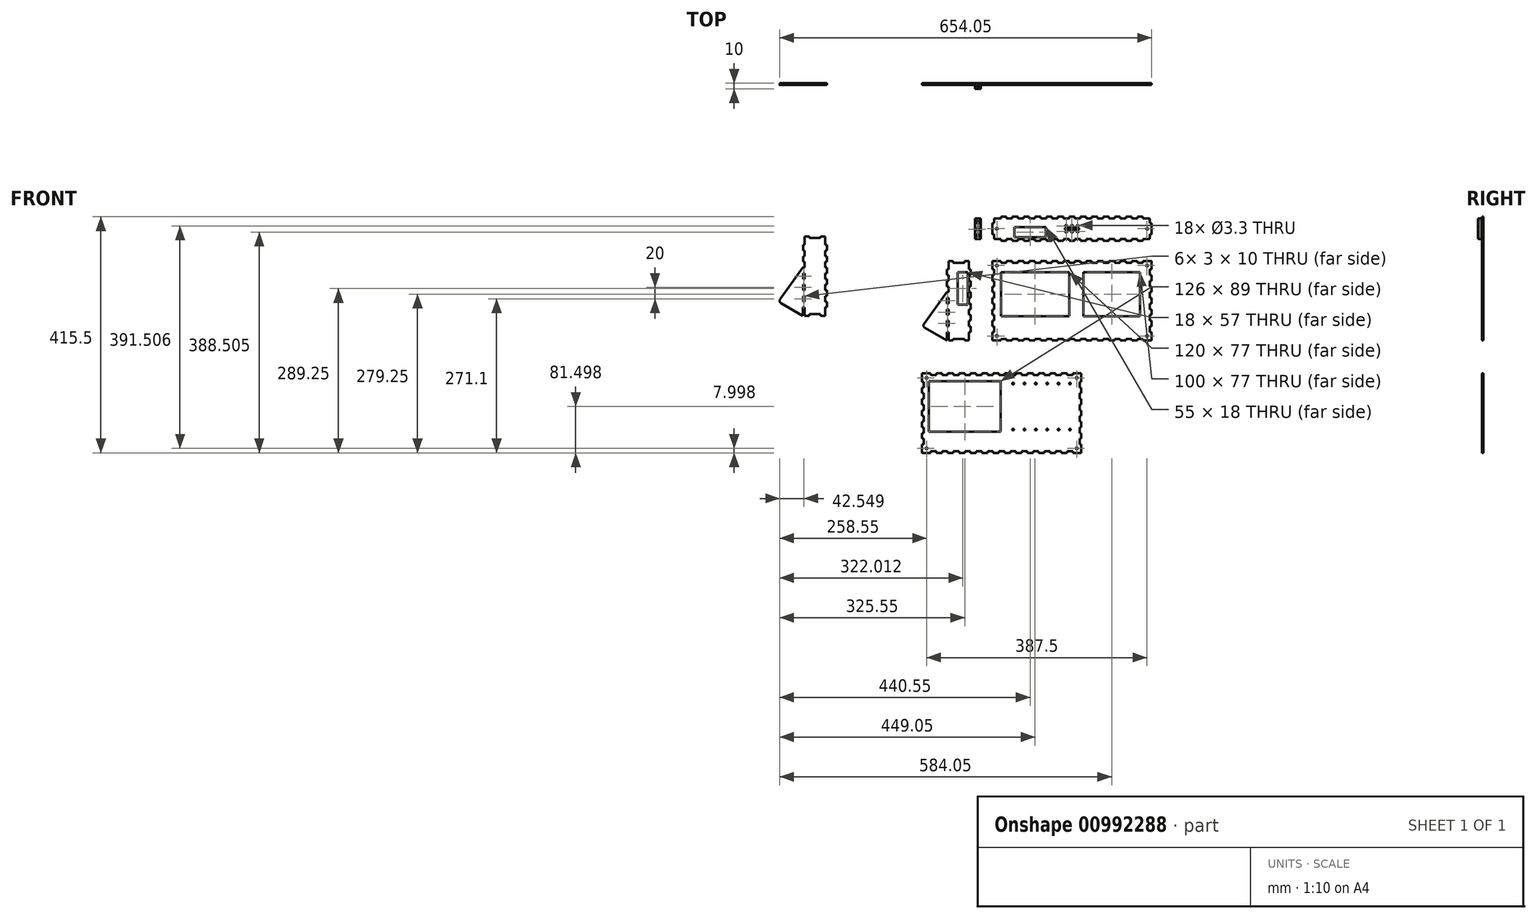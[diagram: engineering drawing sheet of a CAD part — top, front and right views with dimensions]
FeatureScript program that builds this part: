
annotation { "Feature Type Name" : "Feature", "Feature Type Description" : "" }
export const myFeature = defineFeature(function(context is Context, id is Id, definition is map)
    precondition{}
    {
        {
            var Q0;
            Q0=qCreatedBy(makeId("Front.planeOp"),FACE);
            var sketch = newSketch(context, id + "F0", { "sketchPlane" : qUnion([Q0])});
            skLineSegment(sketch, "E0.bottom", {"start": v(-60, 38.5) * mm, "end": v(60, 38.5) * mm});
            skLineSegment(sketch, "E0.top", {"start": v(-60, -38.5) * mm, "end": v(60, -38.5) * mm});
            skLineSegment(sketch, "E0.left", {"start": v(-60, 38.5) * mm, "end": v(-60, -38.5) * mm});
            skLineSegment(sketch, "E0.right", {"start": v(60, 38.5) * mm, "end": v(60, -38.5) * mm});
            skPoint(sketch, "E0.middle", {"position": v(0, 0) * mm});
            skLineSegment(sketch, "E1.bottom", {"start": v(-75, -81.5) * mm, "end": v(-60, -81.5) * mm});
            skLineSegment(sketch, "E1.top", {"start": v(-75, 58.5) * mm, "end": v(-60, 58.5) * mm});
            skLineSegment(sketch, "E1.left", {"start": v(-75, -81.5) * mm, "end": v(-75, -66.5) * mm});
            skLineSegment(sketch, "E1.right", {"start": v(205, -81.5) * mm, "end": v(205, -66.5) * mm});
            skLineSegment(sketch, "E2.bottom", {"start": v(85, -38.5) * mm, "end": v(185, -38.5) * mm});
            skLineSegment(sketch, "E2.top", {"start": v(85, 38.5) * mm, "end": v(185, 38.5) * mm});
            skLineSegment(sketch, "E2.left", {"start": v(85, -38.5) * mm, "end": v(85, 38.5) * mm});
            skLineSegment(sketch, "E2.right", {"start": v(185, -38.5) * mm, "end": v(185, 38.5) * mm});
            skLineSegment(sketch, "E3", {"start": v(-75, 43.5) * mm, "end": v(-72, 43.5) * mm});
            skLineSegment(sketch, "E4", {"start": v(-72, 43.5) * mm, "end": v(-72, 33.5) * mm});
            skLineSegment(sketch, "E5", {"start": v(-72, 33.5) * mm, "end": v(-75, 33.5) * mm});
            skLineSegment(sketch, "E6.0.1.0", {"start": v(-75, 23.5) * mm, "end": v(-72, 23.5) * mm});
            skLineSegment(sketch, "E6.0.1.1", {"start": v(-72, 23.5) * mm, "end": v(-72, 13.5) * mm});
            skLineSegment(sketch, "E6.0.1.2", {"start": v(-72, 13.5) * mm, "end": v(-75, 13.5) * mm});
            skLineSegment(sketch, "E6.0.2.0", {"start": v(-75, 3.5) * mm, "end": v(-72, 3.5) * mm});
            skLineSegment(sketch, "E6.0.2.1", {"start": v(-72, 3.5) * mm, "end": v(-72, -6.5) * mm});
            skLineSegment(sketch, "E6.0.2.2", {"start": v(-72, -6.5) * mm, "end": v(-75, -6.5) * mm});
            skLineSegment(sketch, "E6.0.3.0", {"start": v(-75, -16.5) * mm, "end": v(-72, -16.5) * mm});
            skLineSegment(sketch, "E6.0.3.1", {"start": v(-72, -16.5) * mm, "end": v(-72, -26.5) * mm});
            skLineSegment(sketch, "E6.0.3.2", {"start": v(-72, -26.5) * mm, "end": v(-75, -26.5) * mm});
            skLineSegment(sketch, "E6.0.4.0", {"start": v(-75, -36.5) * mm, "end": v(-72, -36.5) * mm});
            skLineSegment(sketch, "E6.0.4.1", {"start": v(-72, -36.5) * mm, "end": v(-72, -46.5) * mm});
            skLineSegment(sketch, "E6.0.4.2", {"start": v(-72, -46.5) * mm, "end": v(-75, -46.5) * mm});
            skLineSegment(sketch, "E6.0.5.0", {"start": v(-75, -56.5) * mm, "end": v(-72, -56.5) * mm});
            skLineSegment(sketch, "E6.0.5.1", {"start": v(-72, -56.5) * mm, "end": v(-72, -66.5) * mm});
            skLineSegment(sketch, "E6.0.5.2", {"start": v(-72, -66.5) * mm, "end": v(-75, -66.5) * mm});
            skLineSegment(sketch, "E6.direction1", {"start": v(-75, 43.5) * mm, "end": v(-45, 43.5) * mm, "construction": true});
            skLineSegment(sketch, "E6.direction2", {"start": v(-75, 33.5) * mm, "end": v(-75, 23.5) * mm, "construction": true});
            skLineSegment(sketch, "E7", {"start": v(205, 43.5) * mm, "end": v(202, 43.5) * mm});
            skLineSegment(sketch, "E8", {"start": v(202, 43.5) * mm, "end": v(202, 33.5) * mm});
            skLineSegment(sketch, "E9", {"start": v(202, 33.5) * mm, "end": v(205, 33.5) * mm});
            skLineSegment(sketch, "E10.0.1.0", {"start": v(205, 23.5) * mm, "end": v(202, 23.5) * mm});
            skLineSegment(sketch, "E10.0.1.1", {"start": v(202, 23.5) * mm, "end": v(202, 13.5) * mm});
            skLineSegment(sketch, "E10.0.1.2", {"start": v(202, 13.5) * mm, "end": v(205, 13.5) * mm});
            skLineSegment(sketch, "E10.0.2.0", {"start": v(205, 3.5) * mm, "end": v(202, 3.5) * mm});
            skLineSegment(sketch, "E10.0.2.1", {"start": v(202, 3.5) * mm, "end": v(202, -6.5) * mm});
            skLineSegment(sketch, "E10.0.2.2", {"start": v(202, -6.5) * mm, "end": v(205, -6.5) * mm});
            skLineSegment(sketch, "E10.0.3.0", {"start": v(205, -16.5) * mm, "end": v(202, -16.5) * mm});
            skLineSegment(sketch, "E10.0.3.1", {"start": v(202, -16.5) * mm, "end": v(202, -26.5) * mm});
            skLineSegment(sketch, "E10.0.3.2", {"start": v(202, -26.5) * mm, "end": v(205, -26.5) * mm});
            skLineSegment(sketch, "E10.0.4.0", {"start": v(205, -36.5) * mm, "end": v(202, -36.5) * mm});
            skLineSegment(sketch, "E10.0.4.1", {"start": v(202, -36.5) * mm, "end": v(202, -46.5) * mm});
            skLineSegment(sketch, "E10.0.4.2", {"start": v(202, -46.5) * mm, "end": v(205, -46.5) * mm});
            skLineSegment(sketch, "E10.0.5.0", {"start": v(205, -56.5) * mm, "end": v(202, -56.5) * mm});
            skLineSegment(sketch, "E10.0.5.1", {"start": v(202, -56.5) * mm, "end": v(202, -66.5) * mm});
            skLineSegment(sketch, "E10.0.5.2", {"start": v(202, -66.5) * mm, "end": v(205, -66.5) * mm});
            skLineSegment(sketch, "E10.direction1", {"start": v(202, 43.5) * mm, "end": v(232, 43.5) * mm, "construction": true});
            skLineSegment(sketch, "E10.direction2", {"start": v(202, 43.5) * mm, "end": v(202, 23.5) * mm, "construction": true});
            skLineSegment(sketch, "E11", {"start": v(190, -81.5) * mm, "end": v(190, -78.5) * mm});
            skLineSegment(sketch, "E12", {"start": v(190, -78.5) * mm, "end": v(180, -78.5) * mm});
            skLineSegment(sketch, "E13", {"start": v(180, -78.5) * mm, "end": v(180, -81.5) * mm});
            skLineSegment(sketch, "E14.1.0.0", {"start": v(160, -78.5) * mm, "end": v(160, -81.5) * mm});
            skLineSegment(sketch, "E14.1.0.1", {"start": v(170, -78.5) * mm, "end": v(160, -78.5) * mm});
            skLineSegment(sketch, "E14.1.0.2", {"start": v(170, -81.5) * mm, "end": v(170, -78.5) * mm});
            skLineSegment(sketch, "E14.2.0.0", {"start": v(140, -78.5) * mm, "end": v(140, -81.5) * mm});
            skLineSegment(sketch, "E14.2.0.1", {"start": v(150, -78.5) * mm, "end": v(140, -78.5) * mm});
            skLineSegment(sketch, "E14.2.0.2", {"start": v(150, -81.5) * mm, "end": v(150, -78.5) * mm});
            skLineSegment(sketch, "E14.3.0.0", {"start": v(120, -78.5) * mm, "end": v(120, -81.5) * mm});
            skLineSegment(sketch, "E14.3.0.1", {"start": v(130, -78.5) * mm, "end": v(120, -78.5) * mm});
            skLineSegment(sketch, "E14.3.0.2", {"start": v(130, -81.5) * mm, "end": v(130, -78.5) * mm});
            skLineSegment(sketch, "E14.4.0.0", {"start": v(100, -78.5) * mm, "end": v(100, -81.5) * mm});
            skLineSegment(sketch, "E14.4.0.1", {"start": v(110, -78.5) * mm, "end": v(100, -78.5) * mm});
            skLineSegment(sketch, "E14.4.0.2", {"start": v(110, -81.5) * mm, "end": v(110, -78.5) * mm});
            skLineSegment(sketch, "E14.5.0.0", {"start": v(80, -78.5) * mm, "end": v(80, -81.5) * mm});
            skLineSegment(sketch, "E14.5.0.1", {"start": v(90, -78.5) * mm, "end": v(80, -78.5) * mm});
            skLineSegment(sketch, "E14.5.0.2", {"start": v(90, -81.5) * mm, "end": v(90, -78.5) * mm});
            skLineSegment(sketch, "E14.6.0.0", {"start": v(60, -78.5) * mm, "end": v(60, -81.5) * mm});
            skLineSegment(sketch, "E14.6.0.1", {"start": v(70, -78.5) * mm, "end": v(60, -78.5) * mm});
            skLineSegment(sketch, "E14.6.0.2", {"start": v(70, -81.5) * mm, "end": v(70, -78.5) * mm});
            skLineSegment(sketch, "E14.7.0.0", {"start": v(40, -78.5) * mm, "end": v(40, -81.5) * mm});
            skLineSegment(sketch, "E14.7.0.1", {"start": v(50, -78.5) * mm, "end": v(40, -78.5) * mm});
            skLineSegment(sketch, "E14.7.0.2", {"start": v(50, -81.5) * mm, "end": v(50, -78.5) * mm});
            skLineSegment(sketch, "E14.8.0.0", {"start": v(20, -78.5) * mm, "end": v(20, -81.5) * mm});
            skLineSegment(sketch, "E14.8.0.1", {"start": v(30, -78.5) * mm, "end": v(20, -78.5) * mm});
            skLineSegment(sketch, "E14.8.0.2", {"start": v(30, -81.5) * mm, "end": v(30, -78.5) * mm});
            skLineSegment(sketch, "E14.9.0.0", {"start": v(0, -78.5) * mm, "end": v(0, -81.5) * mm});
            skLineSegment(sketch, "E14.9.0.1", {"start": v(10, -78.5) * mm, "end": v(0, -78.5) * mm});
            skLineSegment(sketch, "E14.9.0.2", {"start": v(10, -81.5) * mm, "end": v(10, -78.5) * mm});
            skLineSegment(sketch, "E14.10.0.0", {"start": v(-20, -78.5) * mm, "end": v(-20, -81.5) * mm});
            skLineSegment(sketch, "E14.10.0.1", {"start": v(-10, -78.5) * mm, "end": v(-20, -78.5) * mm});
            skLineSegment(sketch, "E14.10.0.2", {"start": v(-10, -81.5) * mm, "end": v(-10, -78.5) * mm});
            skLineSegment(sketch, "E14.11.0.0", {"start": v(-40, -78.5) * mm, "end": v(-40, -81.5) * mm});
            skLineSegment(sketch, "E14.11.0.1", {"start": v(-30, -78.5) * mm, "end": v(-40, -78.5) * mm});
            skLineSegment(sketch, "E14.11.0.2", {"start": v(-30, -81.5) * mm, "end": v(-30, -78.5) * mm});
            skLineSegment(sketch, "E14.12.0.0", {"start": v(-60, -78.5) * mm, "end": v(-60, -81.5) * mm});
            skLineSegment(sketch, "E14.12.0.1", {"start": v(-50, -78.5) * mm, "end": v(-60, -78.5) * mm});
            skLineSegment(sketch, "E14.12.0.2", {"start": v(-50, -81.5) * mm, "end": v(-50, -78.5) * mm});
            skLineSegment(sketch, "E14.direction1", {"start": v(180, -81.5) * mm, "end": v(170, -81.5) * mm, "construction": true});
            skLineSegment(sketch, "E15", {"start": v(190, 58.5) * mm, "end": v(190, 55.5) * mm});
            skLineSegment(sketch, "E16", {"start": v(190, 55.5) * mm, "end": v(180, 55.5) * mm});
            skLineSegment(sketch, "E17", {"start": v(180, 55.5) * mm, "end": v(180, 58.5) * mm});
            skLineSegment(sketch, "E18.1.0.0", {"start": v(170, 55.5) * mm, "end": v(160, 55.5) * mm});
            skLineSegment(sketch, "E18.1.0.1", {"start": v(170, 58.5) * mm, "end": v(170, 55.5) * mm});
            skLineSegment(sketch, "E18.1.0.2", {"start": v(160, 55.5) * mm, "end": v(160, 58.5) * mm});
            skLineSegment(sketch, "E18.2.0.0", {"start": v(150, 55.5) * mm, "end": v(140, 55.5) * mm});
            skLineSegment(sketch, "E18.2.0.1", {"start": v(150, 58.5) * mm, "end": v(150, 55.5) * mm});
            skLineSegment(sketch, "E18.2.0.2", {"start": v(140, 55.5) * mm, "end": v(140, 58.5) * mm});
            skLineSegment(sketch, "E18.3.0.0", {"start": v(130, 55.5) * mm, "end": v(120, 55.5) * mm});
            skLineSegment(sketch, "E18.3.0.1", {"start": v(130, 58.5) * mm, "end": v(130, 55.5) * mm});
            skLineSegment(sketch, "E18.3.0.2", {"start": v(120, 55.5) * mm, "end": v(120, 58.5) * mm});
            skLineSegment(sketch, "E18.4.0.0", {"start": v(110, 55.5) * mm, "end": v(100, 55.5) * mm});
            skLineSegment(sketch, "E18.4.0.1", {"start": v(110, 58.5) * mm, "end": v(110, 55.5) * mm});
            skLineSegment(sketch, "E18.4.0.2", {"start": v(100, 55.5) * mm, "end": v(100, 58.5) * mm});
            skLineSegment(sketch, "E18.5.0.0", {"start": v(90, 55.5) * mm, "end": v(80, 55.5) * mm});
            skLineSegment(sketch, "E18.5.0.1", {"start": v(90, 58.5) * mm, "end": v(90, 55.5) * mm});
            skLineSegment(sketch, "E18.5.0.2", {"start": v(80, 55.5) * mm, "end": v(80, 58.5) * mm});
            skLineSegment(sketch, "E18.6.0.0", {"start": v(70, 55.5) * mm, "end": v(60, 55.5) * mm});
            skLineSegment(sketch, "E18.6.0.1", {"start": v(70, 58.5) * mm, "end": v(70, 55.5) * mm});
            skLineSegment(sketch, "E18.6.0.2", {"start": v(60, 55.5) * mm, "end": v(60, 58.5) * mm});
            skLineSegment(sketch, "E18.7.0.0", {"start": v(50, 55.5) * mm, "end": v(40, 55.5) * mm});
            skLineSegment(sketch, "E18.7.0.1", {"start": v(50, 58.5) * mm, "end": v(50, 55.5) * mm});
            skLineSegment(sketch, "E18.7.0.2", {"start": v(40, 55.5) * mm, "end": v(40, 58.5) * mm});
            skLineSegment(sketch, "E18.8.0.0", {"start": v(30, 55.5) * mm, "end": v(20, 55.5) * mm});
            skLineSegment(sketch, "E18.8.0.1", {"start": v(30, 58.5) * mm, "end": v(30, 55.5) * mm});
            skLineSegment(sketch, "E18.8.0.2", {"start": v(20, 55.5) * mm, "end": v(20, 58.5) * mm});
            skLineSegment(sketch, "E18.9.0.0", {"start": v(10, 55.5) * mm, "end": v(0, 55.5) * mm});
            skLineSegment(sketch, "E18.9.0.1", {"start": v(10, 58.5) * mm, "end": v(10, 55.5) * mm});
            skLineSegment(sketch, "E18.9.0.2", {"start": v(0, 55.5) * mm, "end": v(0, 58.5) * mm});
            skLineSegment(sketch, "E18.10.0.0", {"start": v(-10, 55.5) * mm, "end": v(-20, 55.5) * mm});
            skLineSegment(sketch, "E18.10.0.1", {"start": v(-10, 58.5) * mm, "end": v(-10, 55.5) * mm});
            skLineSegment(sketch, "E18.10.0.2", {"start": v(-20, 55.5) * mm, "end": v(-20, 58.5) * mm});
            skLineSegment(sketch, "E18.11.0.0", {"start": v(-30, 55.5) * mm, "end": v(-40, 55.5) * mm});
            skLineSegment(sketch, "E18.11.0.1", {"start": v(-30, 58.5) * mm, "end": v(-30, 55.5) * mm});
            skLineSegment(sketch, "E18.11.0.2", {"start": v(-40, 55.5) * mm, "end": v(-40, 58.5) * mm});
            skLineSegment(sketch, "E18.12.0.0", {"start": v(-50, 55.5) * mm, "end": v(-60, 55.5) * mm});
            skLineSegment(sketch, "E18.12.0.1", {"start": v(-50, 58.5) * mm, "end": v(-50, 55.5) * mm});
            skLineSegment(sketch, "E18.12.0.2", {"start": v(-60, 55.5) * mm, "end": v(-60, 58.5) * mm});
            skLineSegment(sketch, "E18.direction1", {"start": v(180, 55.5) * mm, "end": v(160, 55.5) * mm, "construction": true});
            skLineSegment(sketch, "E19.trimOffspring", {"start": v(-50, 58.5) * mm, "end": v(-40, 58.5) * mm});
            skLineSegment(sketch, "E20.trimOffspring", {"start": v(-30, 58.5) * mm, "end": v(-20, 58.5) * mm});
            skLineSegment(sketch, "E21.trimOffspring", {"start": v(-10, 58.5) * mm, "end": v(0, 58.5) * mm});
            skLineSegment(sketch, "E22.trimOffspring", {"start": v(10, 58.5) * mm, "end": v(20, 58.5) * mm});
            skLineSegment(sketch, "E23.trimOffspring", {"start": v(30, 58.5) * mm, "end": v(40, 58.5) * mm});
            skLineSegment(sketch, "E24.trimOffspring", {"start": v(50, 58.5) * mm, "end": v(60, 58.5) * mm});
            skLineSegment(sketch, "E25.trimOffspring", {"start": v(70, 58.5) * mm, "end": v(80, 58.5) * mm});
            skLineSegment(sketch, "E26.trimOffspring", {"start": v(90, 58.5) * mm, "end": v(100, 58.5) * mm});
            skLineSegment(sketch, "E27.trimOffspring", {"start": v(110, 58.5) * mm, "end": v(120, 58.5) * mm});
            skLineSegment(sketch, "E28.trimOffspring", {"start": v(-75, 23.5) * mm, "end": v(-75, 33.5) * mm});
            skLineSegment(sketch, "E29.trimOffspring", {"start": v(130, 58.5) * mm, "end": v(140, 58.5) * mm});
            skLineSegment(sketch, "E30.trimOffspring", {"start": v(150, 58.5) * mm, "end": v(160, 58.5) * mm});
            skLineSegment(sketch, "E31.trimOffspring", {"start": v(170, 58.5) * mm, "end": v(180, 58.5) * mm});
            skLineSegment(sketch, "E32.trimOffspring", {"start": v(190, 58.5) * mm, "end": v(205, 58.5) * mm});
            skLineSegment(sketch, "E33.trimOffspring", {"start": v(205, 43.5) * mm, "end": v(205, 58.5) * mm});
            skLineSegment(sketch, "E34.trimOffspring", {"start": v(205, 23.5) * mm, "end": v(205, 33.5) * mm});
            skLineSegment(sketch, "E35.trimOffspring", {"start": v(205, 3.5) * mm, "end": v(205, 13.5) * mm});
            skLineSegment(sketch, "E36.trimOffspring", {"start": v(205, -16.5) * mm, "end": v(205, -6.5) * mm});
            skLineSegment(sketch, "E37.trimOffspring", {"start": v(205, -56.5) * mm, "end": v(205, -46.5) * mm});
            skLineSegment(sketch, "E38.trimOffspring", {"start": v(205, -36.5) * mm, "end": v(205, -26.5) * mm});
            skLineSegment(sketch, "E39.trimOffspring", {"start": v(190, -81.5) * mm, "end": v(205, -81.5) * mm});
            skLineSegment(sketch, "E40.trimOffspring", {"start": v(150, -81.5) * mm, "end": v(160, -81.5) * mm});
            skLineSegment(sketch, "E41.trimOffspring", {"start": v(130, -81.5) * mm, "end": v(140, -81.5) * mm});
            skLineSegment(sketch, "E42.trimOffspring", {"start": v(110, -81.5) * mm, "end": v(120, -81.5) * mm});
            skLineSegment(sketch, "E43.trimOffspring", {"start": v(170, -81.5) * mm, "end": v(180, -81.5) * mm});
            skLineSegment(sketch, "E44.trimOffspring", {"start": v(90, -81.5) * mm, "end": v(100, -81.5) * mm});
            skLineSegment(sketch, "E45.trimOffspring", {"start": v(70, -81.5) * mm, "end": v(80, -81.5) * mm});
            skLineSegment(sketch, "E46.trimOffspring", {"start": v(50, -81.5) * mm, "end": v(60, -81.5) * mm});
            skLineSegment(sketch, "E47.trimOffspring", {"start": v(30, -81.5) * mm, "end": v(40, -81.5) * mm});
            skLineSegment(sketch, "E48.trimOffspring", {"start": v(10, -81.5) * mm, "end": v(20, -81.5) * mm});
            skLineSegment(sketch, "E49.trimOffspring", {"start": v(-10, -81.5) * mm, "end": v(0, -81.5) * mm});
            skLineSegment(sketch, "E50.trimOffspring", {"start": v(-30, -81.5) * mm, "end": v(-20, -81.5) * mm});
            skLineSegment(sketch, "E51.trimOffspring", {"start": v(-50, -81.5) * mm, "end": v(-40, -81.5) * mm});
            skLineSegment(sketch, "E52.trimOffspring", {"start": v(-75, -56.5) * mm, "end": v(-75, -46.5) * mm});
            skLineSegment(sketch, "E53.trimOffspring", {"start": v(-75, -36.5) * mm, "end": v(-75, -26.5) * mm});
            skLineSegment(sketch, "E54.trimOffspring", {"start": v(-75, -16.5) * mm, "end": v(-75, -6.5) * mm});
            skLineSegment(sketch, "E55.trimOffspring", {"start": v(-75, 3.5) * mm, "end": v(-75, 13.5) * mm});
            skLineSegment(sketch, "E56.trimOffspring", {"start": v(-75, 43.5) * mm, "end": v(-75, 58.5) * mm});
            skLineSegment(sketch, "E57.bottom", {"start": v(-116.04, 58.5) * mm, "end": v(-124.04, 58.5) * mm});
            skLineSegment(sketch, "E57.top", {"start": v(-116.04, -81.5) * mm, "end": v(-124.04, -81.5) * mm});
            skLineSegment(sketch, "E57.left", {"start": v(-116.04, 58.5) * mm, "end": v(-116.04, 43.5) * mm});
            skLineSegment(sketch, "E57.right", {"start": v(-152.04, 58.5) * mm, "end": v(-152.04, 43.5) * mm});
            skLineSegment(sketch, "E58", {"start": v(-116.04, 43.5) * mm, "end": v(-113.04, 43.5) * mm});
            skLineSegment(sketch, "E59", {"start": v(-113.04, 43.5) * mm, "end": v(-113.04, 33.5) * mm});
            skLineSegment(sketch, "E60", {"start": v(-113.04, 33.5) * mm, "end": v(-116.04, 33.5) * mm});
            skLineSegment(sketch, "E61.0.1.0", {"start": v(-116.04, 23.5) * mm, "end": v(-113.04, 23.5) * mm});
            skLineSegment(sketch, "E61.0.1.1", {"start": v(-113.04, 23.5) * mm, "end": v(-113.04, 13.5) * mm});
            skLineSegment(sketch, "E61.0.1.2", {"start": v(-113.04, 13.5) * mm, "end": v(-116.04, 13.5) * mm});
            skLineSegment(sketch, "E61.0.2.0", {"start": v(-116.04, 3.5) * mm, "end": v(-113.04, 3.5) * mm});
            skLineSegment(sketch, "E61.0.2.1", {"start": v(-113.04, 3.5) * mm, "end": v(-113.04, -6.5) * mm});
            skLineSegment(sketch, "E61.0.2.2", {"start": v(-113.04, -6.5) * mm, "end": v(-116.04, -6.5) * mm});
            skLineSegment(sketch, "E61.0.3.0", {"start": v(-116.04, -16.5) * mm, "end": v(-113.04, -16.5) * mm});
            skLineSegment(sketch, "E61.0.3.1", {"start": v(-113.04, -16.5) * mm, "end": v(-113.04, -26.5) * mm});
            skLineSegment(sketch, "E61.0.3.2", {"start": v(-113.04, -26.5) * mm, "end": v(-116.04, -26.5) * mm});
            skLineSegment(sketch, "E61.0.4.0", {"start": v(-116.04, -36.5) * mm, "end": v(-113.04, -36.5) * mm});
            skLineSegment(sketch, "E61.0.4.1", {"start": v(-113.04, -36.5) * mm, "end": v(-113.04, -46.5) * mm});
            skLineSegment(sketch, "E61.0.4.2", {"start": v(-113.04, -46.5) * mm, "end": v(-116.04, -46.5) * mm});
            skLineSegment(sketch, "E61.0.5.0", {"start": v(-116.04, -56.5) * mm, "end": v(-113.04, -56.5) * mm});
            skLineSegment(sketch, "E61.0.5.1", {"start": v(-113.04, -56.5) * mm, "end": v(-113.04, -66.5) * mm});
            skLineSegment(sketch, "E61.0.5.2", {"start": v(-113.04, -66.5) * mm, "end": v(-116.04, -66.5) * mm});
            skLineSegment(sketch, "E61.direction1", {"start": v(-116.04, 43.5) * mm, "end": v(-91.04, 43.5) * mm, "construction": true});
            skLineSegment(sketch, "E61.direction2", {"start": v(-116.04, 33.5) * mm, "end": v(-116.04, 23.5) * mm, "construction": true});
            skLineSegment(sketch, "E62.trimOffspring", {"start": v(-116.04, 13.5) * mm, "end": v(-116.04, 3.5) * mm});
            skLineSegment(sketch, "E63.trimOffspring", {"start": v(-116.04, 33.5) * mm, "end": v(-116.04, 23.5) * mm});
            skLineSegment(sketch, "E64.trimOffspring", {"start": v(-116.04, -6.5) * mm, "end": v(-116.04, -16.5) * mm});
            skLineSegment(sketch, "E65.trimOffspring", {"start": v(-116.04, -26.5) * mm, "end": v(-116.04, -36.5) * mm});
            skLineSegment(sketch, "E66.trimOffspring", {"start": v(-116.04, -46.5) * mm, "end": v(-116.04, -56.5) * mm});
            skLineSegment(sketch, "E67.trimOffspring", {"start": v(-116.04, -66.5) * mm, "end": v(-116.04, -81.5) * mm});
            skLineSegment(sketch, "E68", {"start": v(-152.04, 43.5) * mm, "end": v(-155.04, 43.5) * mm});
            skLineSegment(sketch, "E69", {"start": v(-155.04, 43.5) * mm, "end": v(-155.04, 33.5) * mm});
            skLineSegment(sketch, "E70", {"start": v(-155.04, 33.5) * mm, "end": v(-152.04, 33.5) * mm});
            skLineSegment(sketch, "E71.0.1.0", {"start": v(-152.04, 23.5) * mm, "end": v(-155.04, 23.5) * mm});
            skLineSegment(sketch, "E71.0.1.1", {"start": v(-155.04, 23.5) * mm, "end": v(-155.04, 13.5) * mm});
            skLineSegment(sketch, "E71.0.1.2", {"start": v(-155.04, 13.5) * mm, "end": v(-152.04, 13.5) * mm});
            skLineSegment(sketch, "E71.0.2.0", {"start": v(-152.04, 3.5) * mm, "end": v(-155.04, 3.5) * mm});
            skLineSegment(sketch, "E71.0.2.2", {"start": v(-155.04, -6.5) * mm, "end": v(-152.04, -6.5) * mm});
            skLineSegment(sketch, "E71.0.3.0", {"start": v(-152.04, -16.5) * mm, "end": v(-155.04, -16.5) * mm});
            skLineSegment(sketch, "E71.0.3.2", {"start": v(-155.04, -26.5) * mm, "end": v(-152.04, -26.5) * mm});
            skLineSegment(sketch, "E71.0.4.0", {"start": v(-152.04, -36.5) * mm, "end": v(-155.04, -36.5) * mm});
            skLineSegment(sketch, "E71.0.4.2", {"start": v(-155.04, -46.5) * mm, "end": v(-152.04, -46.5) * mm});
            skLineSegment(sketch, "E71.0.5.0", {"start": v(-152.04, -56.5) * mm, "end": v(-155.04, -56.5) * mm});
            skLineSegment(sketch, "E71.0.5.2", {"start": v(-155.04, -66.5) * mm, "end": v(-152.04, -66.5) * mm});
            skLineSegment(sketch, "E71.direction1", {"start": v(-155.04, 43.5) * mm, "end": v(-130.04, 43.5) * mm, "construction": true});
            skLineSegment(sketch, "E71.direction2", {"start": v(-155.04, 43.5) * mm, "end": v(-155.04, 23.5) * mm, "construction": true});
            skLineSegment(sketch, "E72.trimOffspring", {"start": v(-152.04, 33.5) * mm, "end": v(-152.04, 23.5) * mm});
            skLineSegment(sketch, "E73.trimOffspring", {"start": v(-152.04, 13.5) * mm, "end": v(-152.04, 3.5) * mm});
            skLineSegment(sketch, "E74.trimOffspring", {"start": v(-152.04, -6.5) * mm, "end": v(-152.04, -16.5) * mm});
            skLineSegment(sketch, "E75", {"start": v(-155.04, -66.5) * mm, "end": v(-155.04, -81.5) * mm});
            skLineSegment(sketch, "E76.trimOffspring", {"start": v(-152.04, -66.5) * mm, "end": v(-152.04, -81.5) * mm});
            skLineSegment(sketch, "E77", {"start": v(-155.04, -46.5) * mm, "end": v(-155.04, -56.5) * mm});
            skLineSegment(sketch, "E78", {"start": v(-155.04, -26.5) * mm, "end": v(-155.04, -36.5) * mm});
            skLineSegment(sketch, "E79.trimOffspring", {"start": v(-152.04, -46.5) * mm, "end": v(-152.04, -56.5) * mm});
            skLineSegment(sketch, "E80.trimOffspring", {"start": v(-152.04, -26.5) * mm, "end": v(-152.04, -36.5) * mm});
            skLineSegment(sketch, "E81", {"start": v(-155.04, -81.5) * mm, "end": v(-193.55, -59.27) * mm});
            skLineSegment(sketch, "E82", {"start": v(-155.04, -16.5) * mm, "end": v(-155.04, -6.5) * mm});
            skLineSegment(sketch, "E83", {"start": v(-195.1, -52.01) * mm, "end": v(-155.04, 3.5) * mm});
            skPoint(sketch, "E84.visualSharp", {"position": v(-198.34, -56.5) * mm});
            skArc(sketch, "E84.filletArc", {"start": v(-195.1, -52.01) * mm, "mid": v(-195.93, -55.98) * mm, "end": v(-193.55, -59.27) * mm});
            skLineSegment(sketch, "E85.bottom", {"start": v(-136.04, 38.5) * mm, "end": v(-118.04, 38.5) * mm});
            skLineSegment(sketch, "E85.top", {"start": v(-136.04, -18.5) * mm, "end": v(-118.04, -18.5) * mm});
            skLineSegment(sketch, "E85.left", {"start": v(-136.04, 38.5) * mm, "end": v(-136.04, -18.5) * mm});
            skLineSegment(sketch, "E85.right", {"start": v(-118.04, 38.5) * mm, "end": v(-118.04, -18.5) * mm});
            skLineSegment(sketch, "E86.bottom", {"start": v(-369, 101.85) * mm, "end": v(-377, 101.85) * mm});
            skLineSegment(sketch, "E86.top", {"start": v(-369, -38.15) * mm, "end": v(-377, -38.15) * mm});
            skLineSegment(sketch, "E86.left", {"start": v(-369, 101.85) * mm, "end": v(-369, 86.85) * mm});
            skLineSegment(sketch, "E86.right", {"start": v(-405, 101.85) * mm, "end": v(-405, 86.85) * mm});
            skLineSegment(sketch, "E87", {"start": v(-369, 86.85) * mm, "end": v(-366, 86.85) * mm});
            skLineSegment(sketch, "E88", {"start": v(-366, 86.85) * mm, "end": v(-366, 76.85) * mm});
            skLineSegment(sketch, "E89", {"start": v(-366, 76.85) * mm, "end": v(-369, 76.85) * mm});
            skLineSegment(sketch, "E90.0.1.0", {"start": v(-369, 66.85) * mm, "end": v(-366, 66.85) * mm});
            skLineSegment(sketch, "E90.0.1.1", {"start": v(-366, 66.85) * mm, "end": v(-366, 56.85) * mm});
            skLineSegment(sketch, "E90.0.1.2", {"start": v(-366, 56.85) * mm, "end": v(-369, 56.85) * mm});
            skLineSegment(sketch, "E90.0.2.0", {"start": v(-369, 46.85) * mm, "end": v(-366, 46.85) * mm});
            skLineSegment(sketch, "E90.0.2.1", {"start": v(-366, 46.85) * mm, "end": v(-366, 36.85) * mm});
            skLineSegment(sketch, "E90.0.2.2", {"start": v(-366, 36.85) * mm, "end": v(-369, 36.85) * mm});
            skLineSegment(sketch, "E90.0.3.0", {"start": v(-369, 26.85) * mm, "end": v(-366, 26.85) * mm});
            skLineSegment(sketch, "E90.0.3.1", {"start": v(-366, 26.85) * mm, "end": v(-366, 16.85) * mm});
            skLineSegment(sketch, "E90.0.3.2", {"start": v(-366, 16.85) * mm, "end": v(-369, 16.85) * mm});
            skLineSegment(sketch, "E90.0.4.0", {"start": v(-369, 6.85) * mm, "end": v(-366, 6.85) * mm});
            skLineSegment(sketch, "E90.0.4.1", {"start": v(-366, 6.85) * mm, "end": v(-366, -3.15) * mm});
            skLineSegment(sketch, "E90.0.4.2", {"start": v(-366, -3.15) * mm, "end": v(-369, -3.15) * mm});
            skLineSegment(sketch, "E90.0.5.0", {"start": v(-369, -13.15) * mm, "end": v(-366, -13.15) * mm});
            skLineSegment(sketch, "E90.0.5.1", {"start": v(-366, -13.15) * mm, "end": v(-366, -23.15) * mm});
            skLineSegment(sketch, "E90.0.5.2", {"start": v(-366, -23.15) * mm, "end": v(-369, -23.15) * mm});
            skLineSegment(sketch, "E90.direction2", {"start": v(-369, 76.85) * mm, "end": v(-369, 66.85) * mm, "construction": true});
            skLineSegment(sketch, "E91.trimOffspring", {"start": v(-369, 56.85) * mm, "end": v(-369, 46.85) * mm});
            skLineSegment(sketch, "E92.trimOffspring", {"start": v(-369, 76.85) * mm, "end": v(-369, 66.85) * mm});
            skLineSegment(sketch, "E93.trimOffspring", {"start": v(-369, 36.85) * mm, "end": v(-369, 26.85) * mm});
            skLineSegment(sketch, "E94.trimOffspring", {"start": v(-369, 16.85) * mm, "end": v(-369, 6.85) * mm});
            skLineSegment(sketch, "E95.trimOffspring", {"start": v(-369, -3.15) * mm, "end": v(-369, -13.15) * mm});
            skLineSegment(sketch, "E96.trimOffspring", {"start": v(-369, -23.15) * mm, "end": v(-369, -38.15) * mm});
            skLineSegment(sketch, "E97", {"start": v(-405, 86.85) * mm, "end": v(-408, 86.85) * mm});
            skLineSegment(sketch, "E98", {"start": v(-408, 86.85) * mm, "end": v(-408, 76.85) * mm});
            skLineSegment(sketch, "E99", {"start": v(-408, 76.85) * mm, "end": v(-405, 76.85) * mm});
            skLineSegment(sketch, "E100.0.1.0", {"start": v(-405, 66.85) * mm, "end": v(-408, 66.85) * mm});
            skLineSegment(sketch, "E100.0.1.1", {"start": v(-408, 66.85) * mm, "end": v(-408, 56.85) * mm});
            skLineSegment(sketch, "E100.0.1.2", {"start": v(-408, 56.85) * mm, "end": v(-405, 56.85) * mm});
            skLineSegment(sketch, "E100.0.2.0", {"start": v(-405, 46.85) * mm, "end": v(-408.04, 46.85) * mm});
            skLineSegment(sketch, "E100.0.2.2", {"start": v(-408, 36.85) * mm, "end": v(-405, 36.85) * mm});
            skLineSegment(sketch, "E100.0.3.0", {"start": v(-405, 26.85) * mm, "end": v(-408, 26.85) * mm});
            skLineSegment(sketch, "E100.0.3.2", {"start": v(-408, 16.85) * mm, "end": v(-405, 16.85) * mm});
            skLineSegment(sketch, "E100.0.4.0", {"start": v(-405, 6.85) * mm, "end": v(-408, 6.85) * mm});
            skLineSegment(sketch, "E100.0.4.2", {"start": v(-408, -3.15) * mm, "end": v(-405, -3.15) * mm});
            skLineSegment(sketch, "E100.0.5.0", {"start": v(-405, -13.15) * mm, "end": v(-408, -13.15) * mm});
            skLineSegment(sketch, "E100.0.5.2", {"start": v(-408.04, -23.15) * mm, "end": v(-405, -23.15) * mm});
            skLineSegment(sketch, "E100.direction1", {"start": v(-408, 86.85) * mm, "end": v(-383.04, 86.85) * mm, "construction": true});
            skLineSegment(sketch, "E100.direction2", {"start": v(-408, 86.85) * mm, "end": v(-408, 66.85) * mm, "construction": true});
            skLineSegment(sketch, "E101.trimOffspring", {"start": v(-405, 76.85) * mm, "end": v(-405, 66.85) * mm});
            skLineSegment(sketch, "E102.trimOffspring", {"start": v(-405, 56.85) * mm, "end": v(-405, 46.85) * mm});
            skLineSegment(sketch, "E103.trimOffspring", {"start": v(-405, 36.85) * mm, "end": v(-405, 26.85) * mm});
            skLineSegment(sketch, "E104", {"start": v(-408.04, -23.15) * mm, "end": v(-408.04, -38.15) * mm});
            skLineSegment(sketch, "E105.trimOffspring", {"start": v(-405, -23.15) * mm, "end": v(-405, -38.15) * mm});
            skLineSegment(sketch, "E106", {"start": v(-408, -3.15) * mm, "end": v(-408, -13.15) * mm});
            skLineSegment(sketch, "E107", {"start": v(-408, 16.85) * mm, "end": v(-408, 6.85) * mm});
            skLineSegment(sketch, "E108.trimOffspring", {"start": v(-405, -3.15) * mm, "end": v(-405, -13.15) * mm});
            skLineSegment(sketch, "E109.trimOffspring", {"start": v(-405, 16.85) * mm, "end": v(-405, 6.85) * mm});
            skLineSegment(sketch, "E110", {"start": v(-408.04, -38.15) * mm, "end": v(-446.55, -15.92) * mm});
            skLineSegment(sketch, "E111", {"start": v(-408, 26.85) * mm, "end": v(-408, 36.85) * mm});
            skLineSegment(sketch, "E112", {"start": v(-448.1, -8.66) * mm, "end": v(-408.04, 46.85) * mm});
            skPoint(sketch, "E113.visualSharp", {"position": v(-451.35, -13.15) * mm});
            skArc(sketch, "E113.filletArc", {"start": v(-448.1, -8.66) * mm, "mid": v(-448.94, -12.63) * mm, "end": v(-446.55, -15.92) * mm});
            skLineSegment(sketch, "E114.top", {"start": v(-198.5, -139.25) * mm, "end": v(-183.5, -139.25) * mm});
            skLineSegment(sketch, "E114.left", {"start": v(-198.5, -279.25) * mm, "end": v(-198.5, -264.25) * mm});
            skLineSegment(sketch, "E114.right", {"start": v(81.5, -279.25) * mm, "end": v(81.5, -264.25) * mm});
            skLineSegment(sketch, "E115", {"start": v(-198.5, -154.25) * mm, "end": v(-195.5, -154.25) * mm});
            skLineSegment(sketch, "E116", {"start": v(-195.5, -154.25) * mm, "end": v(-195.5, -164.25) * mm});
            skLineSegment(sketch, "E117", {"start": v(-195.5, -164.25) * mm, "end": v(-198.5, -164.25) * mm});
            skLineSegment(sketch, "E118.0.1.0", {"start": v(-198.5, -174.25) * mm, "end": v(-195.5, -174.25) * mm});
            skLineSegment(sketch, "E118.0.1.1", {"start": v(-195.5, -174.25) * mm, "end": v(-195.5, -184.25) * mm});
            skLineSegment(sketch, "E118.0.1.2", {"start": v(-195.5, -184.25) * mm, "end": v(-198.5, -184.25) * mm});
            skLineSegment(sketch, "E118.0.2.0", {"start": v(-198.5, -194.25) * mm, "end": v(-195.5, -194.25) * mm});
            skLineSegment(sketch, "E118.0.2.1", {"start": v(-195.5, -194.25) * mm, "end": v(-195.5, -204.25) * mm});
            skLineSegment(sketch, "E118.0.2.2", {"start": v(-195.5, -204.25) * mm, "end": v(-198.5, -204.25) * mm});
            skLineSegment(sketch, "E118.0.3.0", {"start": v(-198.5, -214.25) * mm, "end": v(-195.5, -214.25) * mm});
            skLineSegment(sketch, "E118.0.3.1", {"start": v(-195.5, -214.25) * mm, "end": v(-195.5, -224.25) * mm});
            skLineSegment(sketch, "E118.0.3.2", {"start": v(-195.5, -224.25) * mm, "end": v(-198.5, -224.25) * mm});
            skLineSegment(sketch, "E118.0.4.0", {"start": v(-198.5, -234.25) * mm, "end": v(-195.5, -234.25) * mm});
            skLineSegment(sketch, "E118.0.4.1", {"start": v(-195.5, -234.25) * mm, "end": v(-195.5, -244.25) * mm});
            skLineSegment(sketch, "E118.0.4.2", {"start": v(-195.5, -244.25) * mm, "end": v(-198.5, -244.25) * mm});
            skLineSegment(sketch, "E118.0.5.0", {"start": v(-198.5, -254.25) * mm, "end": v(-195.5, -254.25) * mm});
            skLineSegment(sketch, "E118.0.5.1", {"start": v(-195.5, -254.25) * mm, "end": v(-195.5, -264.25) * mm});
            skLineSegment(sketch, "E118.0.5.2", {"start": v(-195.5, -264.25) * mm, "end": v(-198.5, -264.25) * mm});
            skLineSegment(sketch, "E118.direction1", {"start": v(-198.5, -154.25) * mm, "end": v(-170.74, -154.25) * mm, "construction": true});
            skLineSegment(sketch, "E118.direction2", {"start": v(-198.5, -164.25) * mm, "end": v(-198.5, -174.25) * mm, "construction": true});
            skLineSegment(sketch, "E119", {"start": v(81.5, -154.25) * mm, "end": v(78.5, -154.25) * mm});
            skLineSegment(sketch, "E120", {"start": v(78.5, -154.25) * mm, "end": v(78.5, -164.25) * mm});
            skLineSegment(sketch, "E121", {"start": v(78.5, -164.25) * mm, "end": v(81.5, -164.25) * mm});
            skLineSegment(sketch, "E122.0.1.0", {"start": v(81.5, -174.25) * mm, "end": v(78.5, -174.25) * mm});
            skLineSegment(sketch, "E122.0.1.1", {"start": v(78.5, -174.25) * mm, "end": v(78.5, -184.25) * mm});
            skLineSegment(sketch, "E122.0.1.2", {"start": v(78.5, -184.25) * mm, "end": v(81.5, -184.25) * mm});
            skLineSegment(sketch, "E122.0.2.0", {"start": v(81.5, -194.25) * mm, "end": v(78.5, -194.25) * mm});
            skLineSegment(sketch, "E122.0.2.1", {"start": v(78.5, -194.25) * mm, "end": v(78.5, -204.25) * mm});
            skLineSegment(sketch, "E122.0.2.2", {"start": v(78.5, -204.25) * mm, "end": v(81.5, -204.25) * mm});
            skLineSegment(sketch, "E122.0.3.0", {"start": v(81.5, -214.25) * mm, "end": v(78.5, -214.25) * mm});
            skLineSegment(sketch, "E122.0.3.1", {"start": v(78.5, -214.25) * mm, "end": v(78.5, -224.25) * mm});
            skLineSegment(sketch, "E122.0.3.2", {"start": v(78.5, -224.25) * mm, "end": v(81.5, -224.25) * mm});
            skLineSegment(sketch, "E122.0.4.0", {"start": v(81.5, -234.25) * mm, "end": v(78.5, -234.25) * mm});
            skLineSegment(sketch, "E122.0.4.1", {"start": v(78.5, -234.25) * mm, "end": v(78.5, -244.25) * mm});
            skLineSegment(sketch, "E122.0.4.2", {"start": v(78.5, -244.25) * mm, "end": v(81.5, -244.25) * mm});
            skLineSegment(sketch, "E122.0.5.0", {"start": v(81.5, -254.25) * mm, "end": v(78.5, -254.25) * mm});
            skLineSegment(sketch, "E122.0.5.1", {"start": v(78.5, -254.25) * mm, "end": v(78.5, -264.25) * mm});
            skLineSegment(sketch, "E122.0.5.2", {"start": v(78.5, -264.25) * mm, "end": v(81.5, -264.25) * mm});
            skLineSegment(sketch, "E122.direction2", {"start": v(78.5, -154.25) * mm, "end": v(78.5, -174.25) * mm, "construction": true});
            skLineSegment(sketch, "E123", {"start": v(66.5, -279.25) * mm, "end": v(66.5, -276.25) * mm});
            skLineSegment(sketch, "E124", {"start": v(66.5, -276.25) * mm, "end": v(56.5, -276.25) * mm});
            skLineSegment(sketch, "E125", {"start": v(66.5, -139.25) * mm, "end": v(66.5, -142.25) * mm});
            skLineSegment(sketch, "E126", {"start": v(66.5, -142.25) * mm, "end": v(56.5, -142.25) * mm});
            skLineSegment(sketch, "E127", {"start": v(56.5, -142.25) * mm, "end": v(56.5, -139.25) * mm});
            skLineSegment(sketch, "E128.1.0.0", {"start": v(46.5, -142.25) * mm, "end": v(36.5, -142.25) * mm});
            skLineSegment(sketch, "E128.1.0.1", {"start": v(46.5, -139.25) * mm, "end": v(46.5, -142.25) * mm});
            skLineSegment(sketch, "E128.1.0.2", {"start": v(36.5, -142.25) * mm, "end": v(36.5, -139.25) * mm});
            skLineSegment(sketch, "E128.2.0.0", {"start": v(26.5, -142.25) * mm, "end": v(16.5, -142.25) * mm});
            skLineSegment(sketch, "E128.2.0.1", {"start": v(26.5, -139.25) * mm, "end": v(26.5, -142.25) * mm});
            skLineSegment(sketch, "E128.2.0.2", {"start": v(16.5, -142.25) * mm, "end": v(16.5, -139.25) * mm});
            skLineSegment(sketch, "E128.3.0.0", {"start": v(6.5, -142.25) * mm, "end": v(-3.5, -142.25) * mm});
            skLineSegment(sketch, "E128.3.0.1", {"start": v(6.5, -139.25) * mm, "end": v(6.5, -142.25) * mm});
            skLineSegment(sketch, "E128.3.0.2", {"start": v(-3.5, -142.25) * mm, "end": v(-3.5, -139.25) * mm});
            skLineSegment(sketch, "E128.4.0.0", {"start": v(-13.5, -142.25) * mm, "end": v(-23.5, -142.25) * mm});
            skLineSegment(sketch, "E128.4.0.1", {"start": v(-13.5, -139.25) * mm, "end": v(-13.5, -142.25) * mm});
            skLineSegment(sketch, "E128.4.0.2", {"start": v(-23.5, -142.25) * mm, "end": v(-23.5, -139.25) * mm});
            skLineSegment(sketch, "E128.5.0.0", {"start": v(-33.5, -142.25) * mm, "end": v(-43.5, -142.25) * mm});
            skLineSegment(sketch, "E128.5.0.1", {"start": v(-33.5, -139.25) * mm, "end": v(-33.5, -142.25) * mm});
            skLineSegment(sketch, "E128.5.0.2", {"start": v(-43.5, -142.25) * mm, "end": v(-43.5, -139.25) * mm});
            skLineSegment(sketch, "E128.6.0.0", {"start": v(-53.5, -142.25) * mm, "end": v(-63.5, -142.25) * mm});
            skLineSegment(sketch, "E128.6.0.1", {"start": v(-53.5, -139.25) * mm, "end": v(-53.5, -142.25) * mm});
            skLineSegment(sketch, "E128.6.0.2", {"start": v(-63.5, -142.25) * mm, "end": v(-63.5, -139.25) * mm});
            skLineSegment(sketch, "E128.7.0.0", {"start": v(-73.5, -142.25) * mm, "end": v(-83.5, -142.25) * mm});
            skLineSegment(sketch, "E128.7.0.1", {"start": v(-73.5, -139.25) * mm, "end": v(-73.5, -142.25) * mm});
            skLineSegment(sketch, "E128.7.0.2", {"start": v(-83.5, -142.25) * mm, "end": v(-83.5, -139.25) * mm});
            skLineSegment(sketch, "E128.8.0.0", {"start": v(-93.5, -142.25) * mm, "end": v(-103.5, -142.25) * mm});
            skLineSegment(sketch, "E128.8.0.1", {"start": v(-93.5, -139.25) * mm, "end": v(-93.5, -142.25) * mm});
            skLineSegment(sketch, "E128.8.0.2", {"start": v(-103.5, -142.25) * mm, "end": v(-103.5, -139.25) * mm});
            skLineSegment(sketch, "E128.9.0.0", {"start": v(-113.5, -142.25) * mm, "end": v(-123.5, -142.25) * mm});
            skLineSegment(sketch, "E128.9.0.1", {"start": v(-113.5, -139.25) * mm, "end": v(-113.5, -142.25) * mm});
            skLineSegment(sketch, "E128.9.0.2", {"start": v(-123.5, -142.25) * mm, "end": v(-123.5, -139.25) * mm});
            skLineSegment(sketch, "E128.10.0.0", {"start": v(-133.5, -142.25) * mm, "end": v(-143.5, -142.25) * mm});
            skLineSegment(sketch, "E128.10.0.1", {"start": v(-133.5, -139.25) * mm, "end": v(-133.5, -142.25) * mm});
            skLineSegment(sketch, "E128.10.0.2", {"start": v(-143.5, -142.25) * mm, "end": v(-143.5, -139.25) * mm});
            skLineSegment(sketch, "E128.11.0.0", {"start": v(-153.5, -142.25) * mm, "end": v(-163.5, -142.25) * mm});
            skLineSegment(sketch, "E128.11.0.1", {"start": v(-153.5, -139.25) * mm, "end": v(-153.5, -142.25) * mm});
            skLineSegment(sketch, "E128.11.0.2", {"start": v(-163.5, -142.25) * mm, "end": v(-163.5, -139.25) * mm});
            skLineSegment(sketch, "E128.12.0.0", {"start": v(-173.5, -142.25) * mm, "end": v(-183.5, -142.25) * mm});
            skLineSegment(sketch, "E128.12.0.1", {"start": v(-173.5, -139.25) * mm, "end": v(-173.5, -142.25) * mm});
            skLineSegment(sketch, "E128.12.0.2", {"start": v(-183.5, -142.25) * mm, "end": v(-183.5, -139.25) * mm});
            skLineSegment(sketch, "E128.direction1", {"start": v(56.5, -142.25) * mm, "end": v(36.5, -142.25) * mm, "construction": true});
            skLineSegment(sketch, "E129.trimOffspring", {"start": v(-173.5, -139.25) * mm, "end": v(-163.5, -139.25) * mm});
            skLineSegment(sketch, "E130.trimOffspring", {"start": v(-153.5, -139.25) * mm, "end": v(-143.5, -139.25) * mm});
            skLineSegment(sketch, "E131.trimOffspring", {"start": v(-133.5, -139.25) * mm, "end": v(-123.5, -139.25) * mm});
            skLineSegment(sketch, "E132.trimOffspring", {"start": v(-113.5, -139.25) * mm, "end": v(-103.5, -139.25) * mm});
            skLineSegment(sketch, "E133.trimOffspring", {"start": v(-93.5, -139.25) * mm, "end": v(-83.5, -139.25) * mm});
            skLineSegment(sketch, "E134.trimOffspring", {"start": v(-73.5, -139.25) * mm, "end": v(-63.5, -139.25) * mm});
            skLineSegment(sketch, "E135.trimOffspring", {"start": v(-53.5, -139.25) * mm, "end": v(-43.5, -139.25) * mm});
            skLineSegment(sketch, "E136.trimOffspring", {"start": v(-33.5, -139.25) * mm, "end": v(-23.5, -139.25) * mm});
            skLineSegment(sketch, "E137.trimOffspring", {"start": v(-13.5, -139.25) * mm, "end": v(-3.5, -139.25) * mm});
            skLineSegment(sketch, "E138.trimOffspring", {"start": v(-198.5, -174.25) * mm, "end": v(-198.5, -164.25) * mm});
            skLineSegment(sketch, "E139.trimOffspring", {"start": v(6.5, -139.25) * mm, "end": v(16.5, -139.25) * mm});
            skLineSegment(sketch, "E140.trimOffspring", {"start": v(26.5, -139.25) * mm, "end": v(36.5, -139.25) * mm});
            skLineSegment(sketch, "E141.trimOffspring", {"start": v(46.5, -139.25) * mm, "end": v(56.5, -139.25) * mm});
            skLineSegment(sketch, "E142.trimOffspring", {"start": v(66.5, -139.25) * mm, "end": v(81.5, -139.25) * mm});
            skLineSegment(sketch, "E143.trimOffspring", {"start": v(81.5, -154.25) * mm, "end": v(81.5, -139.25) * mm});
            skLineSegment(sketch, "E144.trimOffspring", {"start": v(81.5, -174.25) * mm, "end": v(81.5, -164.25) * mm});
            skLineSegment(sketch, "E145.trimOffspring", {"start": v(81.5, -194.25) * mm, "end": v(81.5, -184.25) * mm});
            skLineSegment(sketch, "E146.trimOffspring", {"start": v(81.5, -214.25) * mm, "end": v(81.5, -204.25) * mm});
            skLineSegment(sketch, "E147.trimOffspring", {"start": v(81.5, -254.25) * mm, "end": v(81.5, -244.25) * mm});
            skLineSegment(sketch, "E148.trimOffspring", {"start": v(81.5, -234.25) * mm, "end": v(81.5, -224.25) * mm});
            skLineSegment(sketch, "E149.trimOffspring", {"start": v(66.5, -279.25) * mm, "end": v(81.5, -279.25) * mm});
            skLineSegment(sketch, "E150.trimOffspring", {"start": v(-198.5, -254.25) * mm, "end": v(-198.5, -244.25) * mm});
            skLineSegment(sketch, "E151.trimOffspring", {"start": v(-198.5, -234.25) * mm, "end": v(-198.5, -224.25) * mm});
            skLineSegment(sketch, "E152.trimOffspring", {"start": v(-198.5, -214.25) * mm, "end": v(-198.5, -204.25) * mm});
            skLineSegment(sketch, "E153.trimOffspring", {"start": v(-198.5, -194.25) * mm, "end": v(-198.5, -184.25) * mm});
            skLineSegment(sketch, "E154.trimOffspring", {"start": v(-198.5, -154.25) * mm, "end": v(-198.5, -139.25) * mm});
            skLineSegment(sketch, "E155.bottom", {"start": v(-60, 94.25) * mm, "end": v(-50, 94.25) * mm});
            skLineSegment(sketch, "E155.top", {"start": v(-60, 136.25) * mm, "end": v(-50, 136.25) * mm});
            skLineSegment(sketch, "E155.left", {"start": v(-75, 105.25) * mm, "end": v(-75, 125.25) * mm});
            skLineSegment(sketch, "E155.right", {"start": v(205, 105.25) * mm, "end": v(205, 125.25) * mm});
            skLineSegment(sketch, "E156", {"start": v(-60, 94.25) * mm, "end": v(-60, 97.25) * mm});
            skLineSegment(sketch, "E157", {"start": v(-60, 97.25) * mm, "end": v(-72, 97.25) * mm});
            skPoint(sketch, "E158.orphan", {"position": v(-75, 94.25) * mm});
            skLineSegment(sketch, "E159", {"start": v(-50, 94.25) * mm, "end": v(-50, 97.25) * mm});
            skLineSegment(sketch, "E160", {"start": v(-50, 97.25) * mm, "end": v(-40, 97.25) * mm});
            skLineSegment(sketch, "E161", {"start": v(-40, 97.25) * mm, "end": v(-40, 94.25) * mm});
            skLineSegment(sketch, "E162.trimOffspring", {"start": v(-40, 94.25) * mm, "end": v(-30, 94.25) * mm});
            skLineSegment(sketch, "E163.1.0.0", {"start": v(-30, 94.25) * mm, "end": v(-30, 97.25) * mm});
            skLineSegment(sketch, "E163.1.0.1", {"start": v(-30, 97.25) * mm, "end": v(-20, 97.25) * mm});
            skLineSegment(sketch, "E163.1.0.2", {"start": v(-20, 97.25) * mm, "end": v(-20, 94.25) * mm});
            skLineSegment(sketch, "E163.2.0.0", {"start": v(-10, 94.25) * mm, "end": v(-10, 97.25) * mm});
            skLineSegment(sketch, "E163.2.0.1", {"start": v(-10, 97.25) * mm, "end": v(0, 97.25) * mm});
            skLineSegment(sketch, "E163.2.0.2", {"start": v(0, 97.25) * mm, "end": v(0, 94.25) * mm});
            skLineSegment(sketch, "E163.3.0.0", {"start": v(10, 94.25) * mm, "end": v(10, 97.25) * mm});
            skLineSegment(sketch, "E163.3.0.1", {"start": v(10, 97.25) * mm, "end": v(20, 97.25) * mm});
            skLineSegment(sketch, "E163.3.0.2", {"start": v(20, 97.25) * mm, "end": v(20, 94.25) * mm});
            skLineSegment(sketch, "E163.4.0.0", {"start": v(30, 94.25) * mm, "end": v(30, 97.25) * mm});
            skLineSegment(sketch, "E163.4.0.1", {"start": v(30, 97.25) * mm, "end": v(40, 97.25) * mm});
            skLineSegment(sketch, "E163.4.0.2", {"start": v(40, 97.25) * mm, "end": v(40, 94.25) * mm});
            skLineSegment(sketch, "E163.5.0.0", {"start": v(50, 94.25) * mm, "end": v(50, 97.25) * mm});
            skLineSegment(sketch, "E163.5.0.1", {"start": v(50, 97.25) * mm, "end": v(60, 97.25) * mm});
            skLineSegment(sketch, "E163.5.0.2", {"start": v(60, 97.25) * mm, "end": v(60, 94.25) * mm});
            skLineSegment(sketch, "E163.6.0.0", {"start": v(70, 94.25) * mm, "end": v(70, 97.25) * mm});
            skLineSegment(sketch, "E163.6.0.1", {"start": v(70, 97.25) * mm, "end": v(80, 97.25) * mm});
            skLineSegment(sketch, "E163.6.0.2", {"start": v(80, 97.25) * mm, "end": v(80, 94.25) * mm});
            skLineSegment(sketch, "E163.7.0.0", {"start": v(90, 94.25) * mm, "end": v(90, 97.25) * mm});
            skLineSegment(sketch, "E163.7.0.1", {"start": v(90, 97.25) * mm, "end": v(100, 97.25) * mm});
            skLineSegment(sketch, "E163.7.0.2", {"start": v(100, 97.25) * mm, "end": v(100, 94.25) * mm});
            skLineSegment(sketch, "E163.8.0.0", {"start": v(110, 94.25) * mm, "end": v(110, 97.25) * mm});
            skLineSegment(sketch, "E163.8.0.1", {"start": v(110, 97.25) * mm, "end": v(120, 97.25) * mm});
            skLineSegment(sketch, "E163.8.0.2", {"start": v(120, 97.25) * mm, "end": v(120, 94.25) * mm});
            skLineSegment(sketch, "E163.9.0.0", {"start": v(130, 94.25) * mm, "end": v(130, 97.25) * mm});
            skLineSegment(sketch, "E163.9.0.1", {"start": v(130, 97.25) * mm, "end": v(140, 97.25) * mm});
            skLineSegment(sketch, "E163.9.0.2", {"start": v(140, 97.25) * mm, "end": v(140, 94.25) * mm});
            skLineSegment(sketch, "E163.10.0.0", {"start": v(150, 94.25) * mm, "end": v(150, 97.25) * mm});
            skLineSegment(sketch, "E163.10.0.1", {"start": v(150, 97.25) * mm, "end": v(160, 97.25) * mm});
            skLineSegment(sketch, "E163.10.0.2", {"start": v(160, 97.25) * mm, "end": v(160, 94.25) * mm});
            skLineSegment(sketch, "E163.11.0.0", {"start": v(170, 94.25) * mm, "end": v(170, 97.25) * mm});
            skLineSegment(sketch, "E163.11.0.1", {"start": v(170, 97.25) * mm, "end": v(180, 97.25) * mm});
            skLineSegment(sketch, "E163.11.0.2", {"start": v(180, 97.25) * mm, "end": v(180, 94.25) * mm});
            skLineSegment(sketch, "E163.direction1", {"start": v(-40, 94.25) * mm, "end": v(-30, 94.25) * mm, "construction": true});
            skLineSegment(sketch, "E164.trimOffspring", {"start": v(-20, 94.25) * mm, "end": v(-10, 94.25) * mm});
            skLineSegment(sketch, "E165.trimOffspring", {"start": v(0, 94.25) * mm, "end": v(10, 94.25) * mm});
            skLineSegment(sketch, "E166.trimOffspring", {"start": v(20, 94.25) * mm, "end": v(30, 94.25) * mm});
            skLineSegment(sketch, "E167.trimOffspring", {"start": v(40, 94.25) * mm, "end": v(50, 94.25) * mm});
            skLineSegment(sketch, "E168.trimOffspring", {"start": v(60, 94.25) * mm, "end": v(70, 94.25) * mm});
            skLineSegment(sketch, "E169.trimOffspring", {"start": v(80, 94.25) * mm, "end": v(90, 94.25) * mm});
            skLineSegment(sketch, "E170.trimOffspring", {"start": v(100, 94.25) * mm, "end": v(110, 94.25) * mm});
            skLineSegment(sketch, "E171.trimOffspring", {"start": v(120, 94.25) * mm, "end": v(130, 94.25) * mm});
            skLineSegment(sketch, "E172.trimOffspring", {"start": v(140, 94.25) * mm, "end": v(150, 94.25) * mm});
            skLineSegment(sketch, "E173.trimOffspring", {"start": v(160, 94.25) * mm, "end": v(170, 94.25) * mm});
            skLineSegment(sketch, "E174.trimOffspring", {"start": v(180, 94.25) * mm, "end": v(190, 94.25) * mm});
            skLineSegment(sketch, "E175", {"start": v(190, 94.25) * mm, "end": v(190, 97.25) * mm});
            skLineSegment(sketch, "E176", {"start": v(190, 97.25) * mm, "end": v(202, 97.25) * mm});
            skLineSegment(sketch, "E177", {"start": v(-60, 136.25) * mm, "end": v(-60, 133.25) * mm});
            skLineSegment(sketch, "E178", {"start": v(-60, 133.25) * mm, "end": v(-72, 133.25) * mm});
            skLineSegment(sketch, "E179", {"start": v(-50, 136.25) * mm, "end": v(-50, 133.25) * mm});
            skLineSegment(sketch, "E180", {"start": v(-50, 133.25) * mm, "end": v(-40, 133.25) * mm});
            skLineSegment(sketch, "E181", {"start": v(-40, 133.25) * mm, "end": v(-40, 136.25) * mm});
            skLineSegment(sketch, "E182.trimOffspring", {"start": v(-40, 136.25) * mm, "end": v(-30, 136.25) * mm});
            skLineSegment(sketch, "E183.1.0.0", {"start": v(-30, 136.25) * mm, "end": v(-30, 133.25) * mm});
            skLineSegment(sketch, "E183.1.0.1", {"start": v(-30, 133.25) * mm, "end": v(-20, 133.25) * mm});
            skLineSegment(sketch, "E183.1.0.2", {"start": v(-20, 133.25) * mm, "end": v(-20, 136.25) * mm});
            skLineSegment(sketch, "E183.2.0.0", {"start": v(-10, 136.25) * mm, "end": v(-10, 133.25) * mm});
            skLineSegment(sketch, "E183.2.0.1", {"start": v(-10, 133.25) * mm, "end": v(0, 133.25) * mm});
            skLineSegment(sketch, "E183.2.0.2", {"start": v(0, 133.25) * mm, "end": v(0, 136.25) * mm});
            skLineSegment(sketch, "E183.3.0.0", {"start": v(10, 136.25) * mm, "end": v(10, 133.25) * mm});
            skLineSegment(sketch, "E183.3.0.1", {"start": v(10, 133.25) * mm, "end": v(20, 133.25) * mm});
            skLineSegment(sketch, "E183.3.0.2", {"start": v(20, 133.25) * mm, "end": v(20, 136.25) * mm});
            skLineSegment(sketch, "E183.4.0.0", {"start": v(30, 136.25) * mm, "end": v(30, 133.25) * mm});
            skLineSegment(sketch, "E183.4.0.1", {"start": v(30, 133.25) * mm, "end": v(40, 133.25) * mm});
            skLineSegment(sketch, "E183.4.0.2", {"start": v(40, 133.25) * mm, "end": v(40, 136.25) * mm});
            skLineSegment(sketch, "E183.5.0.0", {"start": v(50, 136.25) * mm, "end": v(50, 133.25) * mm});
            skLineSegment(sketch, "E183.5.0.1", {"start": v(50, 133.25) * mm, "end": v(60, 133.25) * mm});
            skLineSegment(sketch, "E183.5.0.2", {"start": v(60, 133.25) * mm, "end": v(60, 136.25) * mm});
            skLineSegment(sketch, "E183.6.0.0", {"start": v(70, 136.25) * mm, "end": v(70, 133.25) * mm});
            skLineSegment(sketch, "E183.6.0.1", {"start": v(70, 133.25) * mm, "end": v(80, 133.25) * mm});
            skLineSegment(sketch, "E183.6.0.2", {"start": v(80, 133.25) * mm, "end": v(80, 136.25) * mm});
            skLineSegment(sketch, "E183.7.0.0", {"start": v(90, 136.25) * mm, "end": v(90, 133.25) * mm});
            skLineSegment(sketch, "E183.7.0.1", {"start": v(90, 133.25) * mm, "end": v(100, 133.25) * mm});
            skLineSegment(sketch, "E183.7.0.2", {"start": v(100, 133.25) * mm, "end": v(100, 136.25) * mm});
            skLineSegment(sketch, "E183.8.0.0", {"start": v(110, 136.25) * mm, "end": v(110, 133.25) * mm});
            skLineSegment(sketch, "E183.8.0.1", {"start": v(110, 133.25) * mm, "end": v(120, 133.25) * mm});
            skLineSegment(sketch, "E183.8.0.2", {"start": v(120, 133.25) * mm, "end": v(120, 136.25) * mm});
            skLineSegment(sketch, "E183.9.0.0", {"start": v(130, 136.25) * mm, "end": v(130, 133.25) * mm});
            skLineSegment(sketch, "E183.9.0.1", {"start": v(130, 133.25) * mm, "end": v(140, 133.25) * mm});
            skLineSegment(sketch, "E183.9.0.2", {"start": v(140, 133.25) * mm, "end": v(140, 136.25) * mm});
            skLineSegment(sketch, "E183.10.0.0", {"start": v(150, 136.25) * mm, "end": v(150, 133.25) * mm});
            skLineSegment(sketch, "E183.10.0.1", {"start": v(150, 133.25) * mm, "end": v(160, 133.25) * mm});
            skLineSegment(sketch, "E183.10.0.2", {"start": v(160, 133.25) * mm, "end": v(160, 136.25) * mm});
            skLineSegment(sketch, "E183.11.0.0", {"start": v(170, 136.25) * mm, "end": v(170, 133.25) * mm});
            skLineSegment(sketch, "E183.11.0.1", {"start": v(170, 133.25) * mm, "end": v(180, 133.25) * mm});
            skLineSegment(sketch, "E183.11.0.2", {"start": v(180, 133.25) * mm, "end": v(180, 136.25) * mm});
            skLineSegment(sketch, "E183.direction1", {"start": v(-50, 133.25) * mm, "end": v(-30, 133.25) * mm, "construction": true});
            skLineSegment(sketch, "E184.trimOffspring", {"start": v(-20, 136.25) * mm, "end": v(-10, 136.25) * mm});
            skLineSegment(sketch, "E185.trimOffspring", {"start": v(0, 136.25) * mm, "end": v(10, 136.25) * mm});
            skLineSegment(sketch, "E186.trimOffspring", {"start": v(20, 136.25) * mm, "end": v(30, 136.25) * mm});
            skLineSegment(sketch, "E187.trimOffspring", {"start": v(40, 136.25) * mm, "end": v(50, 136.25) * mm});
            skLineSegment(sketch, "E188.trimOffspring", {"start": v(60, 136.25) * mm, "end": v(70, 136.25) * mm});
            skLineSegment(sketch, "E189.trimOffspring", {"start": v(80, 136.25) * mm, "end": v(90, 136.25) * mm});
            skLineSegment(sketch, "E190.trimOffspring", {"start": v(100, 136.25) * mm, "end": v(110, 136.25) * mm});
            skLineSegment(sketch, "E191.trimOffspring", {"start": v(120, 136.25) * mm, "end": v(130, 136.25) * mm});
            skLineSegment(sketch, "E192.trimOffspring", {"start": v(140, 136.25) * mm, "end": v(150, 136.25) * mm});
            skLineSegment(sketch, "E193.trimOffspring", {"start": v(160, 136.25) * mm, "end": v(170, 136.25) * mm});
            skLineSegment(sketch, "E194.trimOffspring", {"start": v(180, 136.25) * mm, "end": v(190, 136.25) * mm});
            skLineSegment(sketch, "E195", {"start": v(190, 136.25) * mm, "end": v(190, 133.25) * mm});
            skLineSegment(sketch, "E196", {"start": v(190, 133.25) * mm, "end": v(202, 133.25) * mm});
            skPoint(sketch, "E197.orphan", {"position": v(205, 136.25) * mm});
            skLineSegment(sketch, "E198", {"start": v(-144.04, 58.5) * mm, "end": v(-144.04, 55.5) * mm});
            skLineSegment(sketch, "E199", {"start": v(-144.04, 55.5) * mm, "end": v(-124.04, 55.5) * mm});
            skLineSegment(sketch, "E200", {"start": v(-124.04, 55.5) * mm, "end": v(-124.04, 58.5) * mm});
            skLineSegment(sketch, "E201.trimOffspring", {"start": v(-144.04, 58.5) * mm, "end": v(-152.04, 58.5) * mm});
            skLineSegment(sketch, "E202", {"start": v(-144.04, -81.5) * mm, "end": v(-144.04, -78.5) * mm});
            skLineSegment(sketch, "E203", {"start": v(-144.04, -78.5) * mm, "end": v(-124.04, -78.5) * mm});
            skLineSegment(sketch, "E204", {"start": v(-124.04, -78.5) * mm, "end": v(-124.04, -81.5) * mm});
            skLineSegment(sketch, "E205.trimOffspring", {"start": v(-144.04, -81.5) * mm, "end": v(-152.04, -81.5) * mm});
            skLineSegment(sketch, "E206", {"start": v(-72, 133.25) * mm, "end": v(-72, 125.25) * mm});
            skLineSegment(sketch, "E207", {"start": v(-72, 125.25) * mm, "end": v(-75, 125.25) * mm});
            skLineSegment(sketch, "E208", {"start": v(-72, 97.25) * mm, "end": v(-72, 105.25) * mm});
            skLineSegment(sketch, "E209", {"start": v(-72, 105.25) * mm, "end": v(-75, 105.25) * mm});
            skPoint(sketch, "E210.orphan", {"position": v(-75, 97.25) * mm});
            skLineSegment(sketch, "E211", {"start": v(202, 133.25) * mm, "end": v(202, 125.25) * mm});
            skLineSegment(sketch, "E212", {"start": v(202, 125.25) * mm, "end": v(205, 125.25) * mm});
            skLineSegment(sketch, "E213", {"start": v(205, 105.25) * mm, "end": v(202, 105.25) * mm});
            skLineSegment(sketch, "E214", {"start": v(202, 105.25) * mm, "end": v(202, 97.25) * mm});
            skLineSegment(sketch, "E215.bottom", {"start": v(-186.5, -242.25) * mm, "end": v(-60.5, -242.25) * mm});
            skLineSegment(sketch, "E215.top", {"start": v(-186.5, -153.25) * mm, "end": v(-60.5, -153.25) * mm});
            skLineSegment(sketch, "E215.left", {"start": v(-186.5, -242.25) * mm, "end": v(-186.5, -153.25) * mm});
            skLineSegment(sketch, "E215.right", {"start": v(-60.5, -242.25) * mm, "end": v(-60.5, -153.25) * mm});
            skCircle(sketch, "E216", {"center": v(-38.5, -157.25) * mm, "radius": 1.5 * mm});
            skCircle(sketch, "E217.0.1.0", {"center": v(-38.5, -238.25) * mm, "radius": 1.5 * mm});
            skCircle(sketch, "E217.1.0.0", {"center": v(-18.5, -157.25) * mm, "radius": 1.5 * mm});
            skCircle(sketch, "E217.1.1.0", {"center": v(-18.5, -238.25) * mm, "radius": 1.5 * mm});
            skCircle(sketch, "E217.2.0.0", {"center": v(1.5, -157.25) * mm, "radius": 1.5 * mm});
            skCircle(sketch, "E217.2.1.0", {"center": v(1.5, -238.25) * mm, "radius": 1.5 * mm});
            skCircle(sketch, "E217.3.0.0", {"center": v(21.5, -157.25) * mm, "radius": 1.5 * mm});
            skCircle(sketch, "E217.3.1.0", {"center": v(21.5, -238.25) * mm, "radius": 1.5 * mm});
            skCircle(sketch, "E217.4.0.0", {"center": v(41.5, -157.25) * mm, "radius": 1.5 * mm});
            skCircle(sketch, "E217.4.1.0", {"center": v(41.5, -238.25) * mm, "radius": 1.5 * mm});
            skCircle(sketch, "E217.5.0.0", {"center": v(61.5, -157.25) * mm, "radius": 1.5 * mm});
            skCircle(sketch, "E217.5.1.0", {"center": v(61.5, -238.25) * mm, "radius": 1.5 * mm});
            skLineSegment(sketch, "E217.direction1", {"start": v(-38.5, -157.25) * mm, "end": v(-18.5, -157.25) * mm, "construction": true});
            skLineSegment(sketch, "E217.direction2", {"start": v(-38.5, -157.25) * mm, "end": v(-38.5, -238.25) * mm, "construction": true});
            skLineSegment(sketch, "E218.bottom", {"start": v(-36, 118.25) * mm, "end": v(19, 118.25) * mm});
            skLineSegment(sketch, "E218.top", {"start": v(-36, 100.25) * mm, "end": v(19, 100.25) * mm});
            skLineSegment(sketch, "E218.left", {"start": v(-36, 118.25) * mm, "end": v(-36, 100.25) * mm});
            skLineSegment(sketch, "E218.right", {"start": v(19, 118.25) * mm, "end": v(19, 100.25) * mm});
            skCircle(sketch, "E219", {"center": v(55, 120.25) * mm, "radius": 1.65 * mm});
            skCircle(sketch, "E220.0.1.0", {"center": v(55, 110.25) * mm, "radius": 1.65 * mm});
            skCircle(sketch, "E220.1.0.0", {"center": v(65, 120.25) * mm, "radius": 1.65 * mm});
            skCircle(sketch, "E220.1.1.0", {"center": v(65, 110.25) * mm, "radius": 1.65 * mm});
            skCircle(sketch, "E220.2.0.0", {"center": v(75, 120.25) * mm, "radius": 1.65 * mm});
            skCircle(sketch, "E220.2.1.0", {"center": v(75, 110.25) * mm, "radius": 1.65 * mm});
            skLineSegment(sketch, "E220.direction1", {"start": v(55, 120.25) * mm, "end": v(65, 120.25) * mm, "construction": true});
            skLineSegment(sketch, "E220.direction2", {"start": v(55, 120.25) * mm, "end": v(55, 110.25) * mm, "construction": true});
            skLineSegment(sketch, "E221.bottom", {"start": v(52.5, 116.75) * mm, "end": v(77.5, 116.75) * mm});
            skLineSegment(sketch, "E221.top", {"start": v(52.5, 113.75) * mm, "end": v(77.5, 113.75) * mm});
            skLineSegment(sketch, "E221.left", {"start": v(52.5, 116.75) * mm, "end": v(52.5, 113.75) * mm});
            skLineSegment(sketch, "E221.right", {"start": v(77.5, 116.75) * mm, "end": v(77.5, 113.75) * mm});
            skLineSegment(sketch, "E222.direction1", {"start": v(95, -58.5) * mm, "end": v(110.24, -58.5) * mm, "construction": true});
            skLineSegment(sketch, "E223", {"start": v(56.5, -276.25) * mm, "end": v(56.5, -279.25) * mm});
            skLineSegment(sketch, "E224", {"start": v(56.5, -279.25) * mm, "end": v(46.5, -279.25) * mm});
            skLineSegment(sketch, "E225.1.0.0", {"start": v(46.5, -279.25) * mm, "end": v(46.5, -276.25) * mm});
            skLineSegment(sketch, "E225.1.0.1", {"start": v(46.5, -276.25) * mm, "end": v(36.5, -276.25) * mm});
            skLineSegment(sketch, "E225.1.0.2", {"start": v(36.5, -276.25) * mm, "end": v(36.5, -279.25) * mm});
            skLineSegment(sketch, "E225.1.0.3", {"start": v(36.5, -279.25) * mm, "end": v(26.5, -279.25) * mm});
            skLineSegment(sketch, "E225.2.0.0", {"start": v(26.5, -279.25) * mm, "end": v(26.5, -276.25) * mm});
            skLineSegment(sketch, "E225.2.0.1", {"start": v(26.5, -276.25) * mm, "end": v(16.5, -276.25) * mm});
            skLineSegment(sketch, "E225.2.0.2", {"start": v(16.5, -276.25) * mm, "end": v(16.5, -279.25) * mm});
            skLineSegment(sketch, "E225.2.0.3", {"start": v(16.5, -279.25) * mm, "end": v(6.5, -279.25) * mm});
            skLineSegment(sketch, "E225.3.0.0", {"start": v(6.5, -279.25) * mm, "end": v(6.5, -276.25) * mm});
            skLineSegment(sketch, "E225.3.0.1", {"start": v(6.5, -276.25) * mm, "end": v(-3.5, -276.25) * mm});
            skLineSegment(sketch, "E225.3.0.2", {"start": v(-3.5, -276.25) * mm, "end": v(-3.5, -279.25) * mm});
            skLineSegment(sketch, "E225.3.0.3", {"start": v(-3.5, -279.25) * mm, "end": v(-13.5, -279.25) * mm});
            skLineSegment(sketch, "E225.4.0.0", {"start": v(-13.5, -279.25) * mm, "end": v(-13.5, -276.25) * mm});
            skLineSegment(sketch, "E225.4.0.1", {"start": v(-13.5, -276.25) * mm, "end": v(-23.5, -276.25) * mm});
            skLineSegment(sketch, "E225.4.0.2", {"start": v(-23.5, -276.25) * mm, "end": v(-23.5, -279.25) * mm});
            skLineSegment(sketch, "E225.4.0.3", {"start": v(-23.5, -279.25) * mm, "end": v(-33.5, -279.25) * mm});
            skLineSegment(sketch, "E225.5.0.0", {"start": v(-33.5, -279.25) * mm, "end": v(-33.5, -276.25) * mm});
            skLineSegment(sketch, "E225.5.0.1", {"start": v(-33.5, -276.25) * mm, "end": v(-43.5, -276.25) * mm});
            skLineSegment(sketch, "E225.5.0.2", {"start": v(-43.5, -276.25) * mm, "end": v(-43.5, -279.25) * mm});
            skLineSegment(sketch, "E225.5.0.3", {"start": v(-43.5, -279.25) * mm, "end": v(-53.5, -279.25) * mm});
            skLineSegment(sketch, "E225.6.0.0", {"start": v(-53.5, -279.25) * mm, "end": v(-53.5, -276.25) * mm});
            skLineSegment(sketch, "E225.6.0.1", {"start": v(-53.5, -276.25) * mm, "end": v(-63.5, -276.25) * mm});
            skLineSegment(sketch, "E225.6.0.2", {"start": v(-63.5, -276.25) * mm, "end": v(-63.5, -279.25) * mm});
            skLineSegment(sketch, "E225.6.0.3", {"start": v(-63.5, -279.25) * mm, "end": v(-73.5, -279.25) * mm});
            skLineSegment(sketch, "E225.7.0.0", {"start": v(-73.5, -279.25) * mm, "end": v(-73.5, -276.25) * mm});
            skLineSegment(sketch, "E225.7.0.1", {"start": v(-73.5, -276.25) * mm, "end": v(-83.5, -276.25) * mm});
            skLineSegment(sketch, "E225.7.0.2", {"start": v(-83.5, -276.25) * mm, "end": v(-83.5, -279.25) * mm});
            skLineSegment(sketch, "E225.7.0.3", {"start": v(-83.5, -279.25) * mm, "end": v(-93.5, -279.25) * mm});
            skLineSegment(sketch, "E225.8.0.0", {"start": v(-93.5, -279.25) * mm, "end": v(-93.5, -276.25) * mm});
            skLineSegment(sketch, "E225.8.0.1", {"start": v(-93.5, -276.25) * mm, "end": v(-103.5, -276.25) * mm});
            skLineSegment(sketch, "E225.8.0.2", {"start": v(-103.5, -276.25) * mm, "end": v(-103.5, -279.25) * mm});
            skLineSegment(sketch, "E225.8.0.3", {"start": v(-103.5, -279.25) * mm, "end": v(-113.5, -279.25) * mm});
            skLineSegment(sketch, "E225.9.0.0", {"start": v(-113.5, -279.25) * mm, "end": v(-113.5, -276.25) * mm});
            skLineSegment(sketch, "E225.9.0.1", {"start": v(-113.5, -276.25) * mm, "end": v(-123.5, -276.25) * mm});
            skLineSegment(sketch, "E225.9.0.2", {"start": v(-123.5, -276.25) * mm, "end": v(-123.5, -279.25) * mm});
            skLineSegment(sketch, "E225.9.0.3", {"start": v(-123.5, -279.25) * mm, "end": v(-133.5, -279.25) * mm});
            skLineSegment(sketch, "E225.10.0.0", {"start": v(-133.5, -279.25) * mm, "end": v(-133.5, -276.25) * mm});
            skLineSegment(sketch, "E225.10.0.1", {"start": v(-133.5, -276.25) * mm, "end": v(-143.5, -276.25) * mm});
            skLineSegment(sketch, "E225.10.0.2", {"start": v(-143.5, -276.25) * mm, "end": v(-143.5, -279.25) * mm});
            skLineSegment(sketch, "E225.10.0.3", {"start": v(-143.5, -279.25) * mm, "end": v(-153.5, -279.25) * mm});
            skLineSegment(sketch, "E225.11.0.0", {"start": v(-153.5, -279.25) * mm, "end": v(-153.5, -276.25) * mm});
            skLineSegment(sketch, "E225.11.0.1", {"start": v(-153.5, -276.25) * mm, "end": v(-163.5, -276.25) * mm});
            skLineSegment(sketch, "E225.11.0.2", {"start": v(-163.5, -276.25) * mm, "end": v(-163.5, -279.25) * mm});
            skLineSegment(sketch, "E225.11.0.3", {"start": v(-163.5, -279.25) * mm, "end": v(-173.5, -279.25) * mm});
            skLineSegment(sketch, "E225.12.0.0", {"start": v(-173.5, -279.25) * mm, "end": v(-173.5, -276.25) * mm});
            skLineSegment(sketch, "E225.12.0.1", {"start": v(-173.5, -276.25) * mm, "end": v(-183.5, -276.25) * mm});
            skLineSegment(sketch, "E225.12.0.2", {"start": v(-183.5, -276.25) * mm, "end": v(-183.5, -279.25) * mm});
            skLineSegment(sketch, "E225.12.0.3", {"start": v(-183.5, -279.25) * mm, "end": v(-193.5, -279.25) * mm});
            skLineSegment(sketch, "E225.direction1", {"start": v(66.5, -279.25) * mm, "end": v(46.5, -279.25) * mm, "construction": true});
            skLineSegment(sketch, "E226", {"start": v(-198.5, -279.25) * mm, "end": v(-193.5, -279.25) * mm});
            skCircle(sketch, "E227", {"center": v(-190.5, -147.25) * mm, "radius": 1.65 * mm});
            skCircle(sketch, "E228", {"center": v(-190.5, -271.25) * mm, "radius": 1.65 * mm});
            skCircle(sketch, "E229", {"center": v(73.5, -271.25) * mm, "radius": 1.65 * mm});
            skCircle(sketch, "E230", {"center": v(73.5, -147.25) * mm, "radius": 1.65 * mm});
            skCircle(sketch, "E231", {"center": v(-67, -73.5) * mm, "radius": 1.65 * mm});
            skCircle(sketch, "E232", {"center": v(-67, 50.5) * mm, "radius": 1.65 * mm});
            skCircle(sketch, "E233", {"center": v(197, 50.5) * mm, "radius": 1.65 * mm});
            skCircle(sketch, "E234", {"center": v(197, -73.5) * mm, "radius": 1.65 * mm});
            skCircle(sketch, "E235", {"center": v(-67, 115.25) * mm, "radius": 1.65 * mm});
            skCircle(sketch, "E236", {"center": v(197, 115.25) * mm, "radius": 1.65 * mm});
            skLineSegment(sketch, "E237.bottom", {"start": v(-95.17, 133.25) * mm, "end": v(-105.17, 133.25) * mm});
            skLineSegment(sketch, "E237.top", {"start": v(-95.17, 97.25) * mm, "end": v(-105.17, 97.25) * mm});
            skLineSegment(sketch, "E237.left", {"start": v(-95.17, 133.25) * mm, "end": v(-95.17, 97.25) * mm});
            skLineSegment(sketch, "E237.right", {"start": v(-105.17, 133.25) * mm, "end": v(-105.17, 97.25) * mm});
            skLineSegment(sketch, "E238", {"start": v(-397, -38.15) * mm, "end": v(-397, -35.15) * mm});
            skLineSegment(sketch, "E239", {"start": v(-397, -35.15) * mm, "end": v(-377, -35.15) * mm});
            skLineSegment(sketch, "E240", {"start": v(-377, -35.15) * mm, "end": v(-377, -38.15) * mm});
            skLineSegment(sketch, "E241.trimOffspring", {"start": v(-397, -38.15) * mm, "end": v(-405, -38.15) * mm});
            skLineSegment(sketch, "E242", {"start": v(-397, 101.85) * mm, "end": v(-397, 98.85) * mm});
            skLineSegment(sketch, "E243", {"start": v(-397, 98.85) * mm, "end": v(-377, 98.85) * mm});
            skLineSegment(sketch, "E244", {"start": v(-377, 98.85) * mm, "end": v(-377, 101.85) * mm});
            skLineSegment(sketch, "E245.trimOffspring", {"start": v(-397, 101.85) * mm, "end": v(-405, 101.85) * mm});
            skSolve(sketch);
        }
        {
            var Q0;
            Q0=makeQuery(id+"F0.imprint","IMPRINT",FACE,{"disambiguationData":[TD([[makeQuery(id+"F0.imprint","IMPRINT",EDGE,{"derivedFrom":sQuery(id+"F0.wireOp",EDGE,"E86.bottom")}),1.0]])]});
            var Q1;
            Q1=makeQuery(id+"F0.imprint","IMPRINT",FACE,{"disambiguationData":[TD([[makeQuery(id+"F0.imprint","IMPRINT",EDGE,{"derivedFrom":sQuery(id+"F0.wireOp",EDGE,"E57.bottom")}),1.0]])]});
            var Q2;
            Q2=makeQuery(id+"F0.imprint","IMPRINT",FACE,{"disambiguationData":[TD([[makeQuery(id+"F0.imprint","IMPRINT",EDGE,{"derivedFrom":sQuery(id+"F0.wireOp",EDGE,"E0.bottom")}),1.0]])]});
            var Q3;
            Q3=makeQuery(id+"F0.imprint","IMPRINT",FACE,{"disambiguationData":[TD([[makeQuery(id+"F0.imprint","IMPRINT",EDGE,{"derivedFrom":sQuery(id+"F0.wireOp",EDGE,"E155.bottom")}),1.0]])]});
            var Q4;
            Q4=makeQuery(id+"F0.imprint","IMPRINT",FACE,{"disambiguationData":[TD([[makeQuery(id+"F0.imprint","IMPRINT",EDGE,{"derivedFrom":sQuery(id+"F0.wireOp",EDGE,"E114.top")}),-1.0]])]});
            extrude(context, id + "F1", {"entities" : qUnion([Q0, Q1, Q2, Q3, Q4]), "depth" : 3 * mm, "offsetDistance" : 25 * mm});
        }
        {
            var Q0;
            Q0=makeQuery(id+"F0.imprint","IMPRINT",FACE,{"disambiguationData":[TD([[makeQuery(id+"F0.imprint","IMPRINT",EDGE,{"derivedFrom":sQuery(id+"F0.wireOp",EDGE,"E237.bottom")}),1.0]])]});
            extrude(context, id + "F2", {"entities" : qUnion([Q0]), "depth" : 10 * mm, "offsetDistance" : 25 * mm});
        }
        {
            var Q0;
            Q0=makeQuery(id+"F2.opExtrude","CAP_FACE",FACE,{"disambiguationData":[OSD([sQuery(id+"F0.wireOp",EDGE,"E237.bottom"),sQuery(id+"F0.wireOp",EDGE,"E237.top"),sQuery(id+"F0.wireOp",EDGE,"E237.left"),sQuery(id+"F0.wireOp",EDGE,"E237.right")])],"isStart":false});
            var sketch = newSketch(context, id + "F3", { "sketchPlane" : qUnion([Q0])});
            skCircle(sketch, "E246", {"center": v(-100.17, 114.25) * mm, "radius": 1.65 * mm});
            skSolve(sketch);
        }
        {
            var Q0;
            Q0=makeQuery(id+"F3.imprint","IMPRINT",FACE,{"disambiguationData":[TD([[makeQuery(id+"F3.imprint","IMPRINT",EDGE,{"derivedFrom":sQuery(id+"F3.wireOp",EDGE,"E246")}),1.0]])]});
            extrude(context, id + "F4", {"entities" : qUnion([Q0]), "operationType" : NewBodyOperationType.REMOVE, "oppositeDirection" : true, "depth" : 10 * mm, "offsetDistance" : 25 * mm});
        }
        {
            var Q0;
            Q0=makeQuery(id+"F2.opExtrude","CAP_FACE",FACE,{"disambiguationData":[OSD([sQuery(id+"F0.wireOp",EDGE,"E237.bottom"),sQuery(id+"F0.wireOp",EDGE,"E237.top"),sQuery(id+"F0.wireOp",EDGE,"E237.left"),sQuery(id+"F0.wireOp",EDGE,"E237.right")])],"isStart":true});
            var sketch = newSketch(context, id + "F5", { "sketchPlane" : qUnion([Q0])});
            skCircle(sketch, "E247.cCircle", {"center": v(100.17, 114.25) * mm, "radius": 2.75 * mm, "construction": true});
            skLineSegment(sketch, "E247.0", {"start": v(97.42, 112.67) * mm, "end": v(97.42, 115.84) * mm});
            skLineSegment(sketch, "E247.1", {"start": v(97.42, 115.84) * mm, "end": v(100.17, 117.43) * mm});
            skLineSegment(sketch, "E247.2", {"start": v(100.17, 117.43) * mm, "end": v(102.92, 115.84) * mm});
            skLineSegment(sketch, "E247.3", {"start": v(102.92, 115.84) * mm, "end": v(102.92, 112.67) * mm});
            skLineSegment(sketch, "E247.4", {"start": v(102.92, 112.67) * mm, "end": v(100.17, 111.08) * mm});
            skLineSegment(sketch, "E247.5", {"start": v(100.17, 111.08) * mm, "end": v(97.42, 112.67) * mm});
            skPoint(sketch, "E247.0.midPoint", {"position": v(97.42, 114.25) * mm});
            skSolve(sketch);
        }
        {
            var Q0;
            Q0=makeQuery(id+"F5.imprint","IMPRINT",FACE,{"disambiguationData":[TD([[makeQuery(id+"F5.imprint","IMPRINT",EDGE,{"derivedFrom":makeQuery(id+"F4.boolean.opBoolean","COPY",EDGE,{"derivedFrom":makeQuery(id+"F4.opExtrude","CAP_EDGE",EDGE,{"disambiguationData":[OSD([sQuery(id+"F3.wireOp",EDGE,"E246")])],"isStart":false})})}),-1.0]])]});
            var Q1;
            Q1=makeQuery(id+"F5.imprint","IMPRINT",FACE,{"disambiguationData":[TD([[makeQuery(id+"F5.imprint","IMPRINT",EDGE,{"derivedFrom":sQuery(id+"F5.wireOp",EDGE,"E247.0")}),-1.0]])]});
            extrude(context, id + "F6", {"entities" : qUnion([Q0, Q1]), "operationType" : NewBodyOperationType.REMOVE, "oppositeDirection" : true, "depth" : 3 * mm, "offsetDistance" : 25 * mm});
        }
        {
            var Q0;
            Q0=makeQuery(id+"F2.opExtrude","SWEPT_FACE",FACE,{"disambiguationData":[OSD([sQuery(id+"F0.wireOp",EDGE,"E237.top")])]});
            var sketch = newSketch(context, id + "F7", { "sketchPlane" : qUnion([Q0])});
            skCircle(sketch, "E248", {"center": v(-100.17, 5) * mm, "radius": 1.65 * mm});
            skSolve(sketch);
        }
        {
            var Q0;
            Q0=qSketchRegion(id+"F7",true);
            extrude(context, id + "F8", {"entities" : qUnion([Q0]), "operationType" : NewBodyOperationType.REMOVE, "oppositeDirection" : true, "depth" : 36 * mm, "offsetDistance" : 25 * mm});
        }
        {
            var Q0;
            Q0=makeQuery(id+"F2.opExtrude","CAP_FACE",FACE,{"disambiguationData":[OSD([sQuery(id+"F0.wireOp",EDGE,"E237.bottom"),sQuery(id+"F0.wireOp",EDGE,"E237.top"),sQuery(id+"F0.wireOp",EDGE,"E237.left"),sQuery(id+"F0.wireOp",EDGE,"E237.right")])],"isStart":true});
            var sketch = newSketch(context, id + "F9", { "sketchPlane" : qUnion([Q0])});
            skLineSegment(sketch, "E249.bottom", {"start": v(97.07, 128.25) * mm, "end": v(103.27, 128.25) * mm});
            skLineSegment(sketch, "E249.top", {"start": v(97.07, 125.85) * mm, "end": v(103.27, 125.85) * mm});
            skLineSegment(sketch, "E249.left", {"start": v(97.07, 128.25) * mm, "end": v(97.07, 125.85) * mm});
            skLineSegment(sketch, "E249.right", {"start": v(103.27, 128.25) * mm, "end": v(103.27, 125.85) * mm});
            skLineSegment(sketch, "E250.bottom", {"start": v(97.07, 104.65) * mm, "end": v(103.27, 104.65) * mm});
            skLineSegment(sketch, "E250.top", {"start": v(97.07, 102.25) * mm, "end": v(103.27, 102.25) * mm});
            skLineSegment(sketch, "E250.left", {"start": v(97.07, 104.65) * mm, "end": v(97.07, 102.25) * mm});
            skLineSegment(sketch, "E250.right", {"start": v(103.27, 104.65) * mm, "end": v(103.27, 102.25) * mm});
            skSolve(sketch);
        }
        {
            var Q0;
            Q0=makeQuery(id+"F9.imprint","IMPRINT",FACE,{"disambiguationData":[TD([[makeQuery(id+"F9.imprint","IMPRINT",EDGE,{"derivedFrom":sQuery(id+"F9.wireOp",EDGE,"E250.bottom")}),-1.0]])]});
            var Q1;
            Q1=makeQuery(id+"F9.imprint","IMPRINT",FACE,{"disambiguationData":[TD([[makeQuery(id+"F9.imprint","IMPRINT",EDGE,{"derivedFrom":sQuery(id+"F9.wireOp",EDGE,"E249.bottom")}),-1.0]])]});
            extrude(context, id + "F10", {"entities" : qUnion([Q0, Q1]), "operationType" : NewBodyOperationType.REMOVE, "oppositeDirection" : true, "depth" : 10 * mm, "offsetDistance" : 25 * mm});
        }
    });
